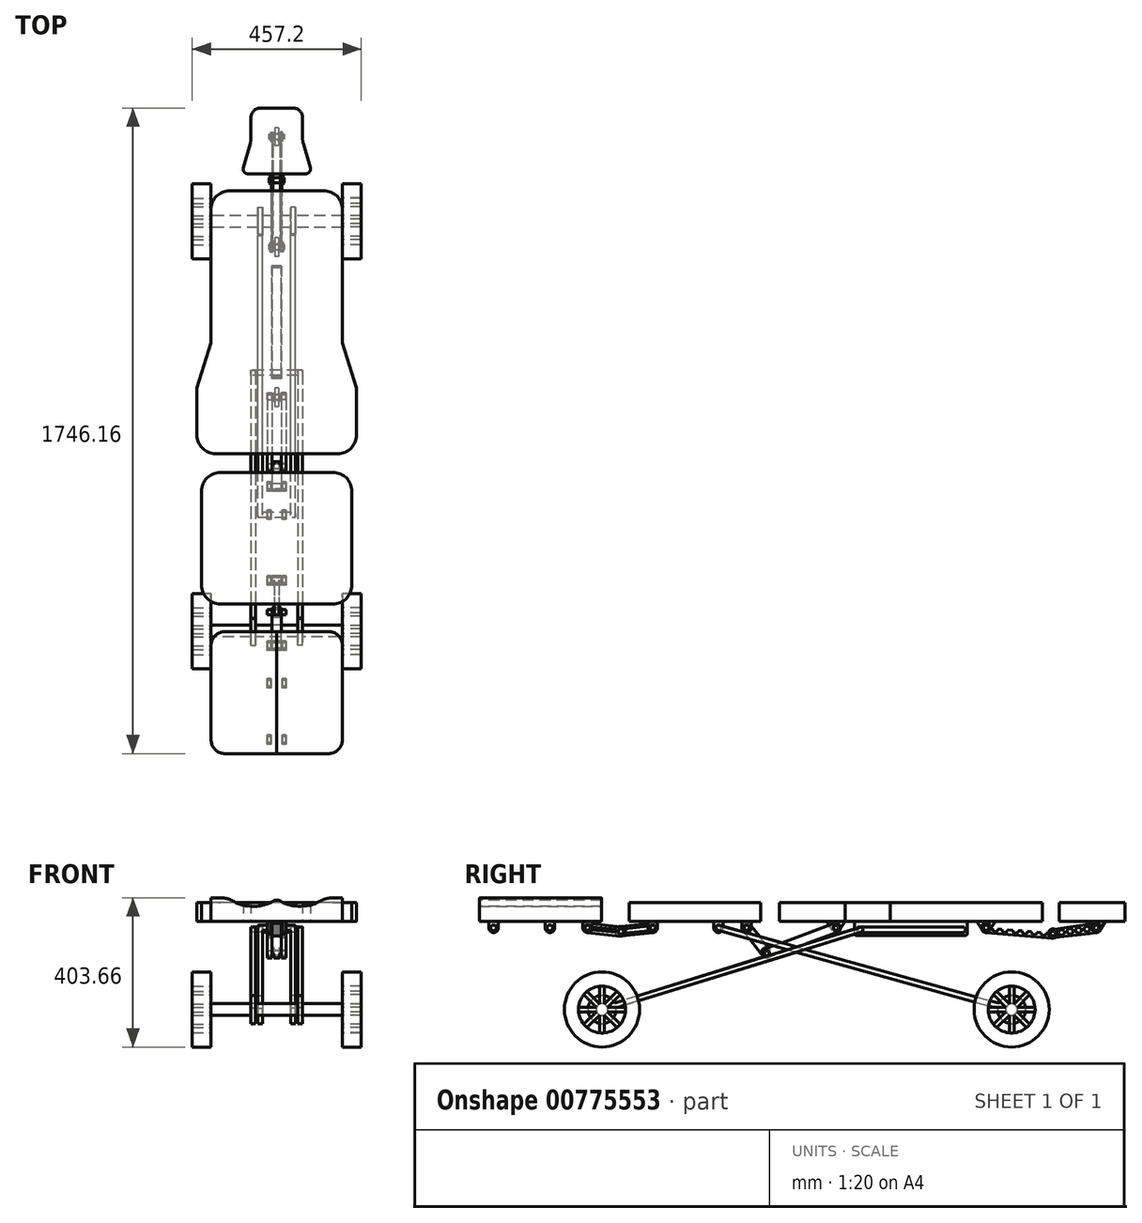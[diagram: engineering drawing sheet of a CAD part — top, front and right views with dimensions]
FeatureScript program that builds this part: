
annotation { "Feature Type Name" : "Feature", "Feature Type Description" : "" }
export const myFeature = defineFeature(function(context is Context, id is Id, definition is map)
    precondition{}
    {
        {
            var Q0;
            Q0=qCreatedBy(makeId("Top.planeOp"),FACE);
            var sketch = newSketch(context, id + "F0", { "sketchPlane" : qUnion([Q0])});
            skLineSegment(sketch, "E0.top", {"start": v(165.1, -355.6) * mm, "end": v(-165.1, -355.6) * mm});
            skLineSegment(sketch, "E0.left", {"start": v(215.9, -177.8) * mm, "end": v(215.9, -304.8) * mm});
            skLineSegment(sketch, "E0.right", {"start": v(-215.9, -177.8) * mm, "end": v(-215.9, -304.8) * mm});
            skPoint(sketch, "E0.middle", {"position": v(0, 0) * mm});
            skLineSegment(sketch, "E1.bottom", {"start": v(127, 355.6) * mm, "end": v(-127, 355.6) * mm});
            skLineSegment(sketch, "E1.left", {"start": v(177.8, 304.8) * mm, "end": v(177.8, -56.4) * mm});
            skLineSegment(sketch, "E1.right", {"start": v(-177.8, 304.8) * mm, "end": v(-177.8, -56.4) * mm});
            skPoint(sketch, "E2.orphan", {"position": v(-177.8, -355.6) * mm});
            skPoint(sketch, "E3.orphan", {"position": v(177.8, -355.6) * mm});
            skPoint(sketch, "E4.orphan", {"position": v(-215.9, 355.6) * mm});
            skPoint(sketch, "E5.orphan", {"position": v(215.9, 355.6) * mm});
            skPoint(sketch, "E6.visualSharp", {"position": v(-215.9, -355.6) * mm});
            skArc(sketch, "E6.filletArc", {"start": v(-215.9, -304.8) * mm, "mid": v(-201.02, -340.72) * mm, "end": v(-165.1, -355.6) * mm});
            skPoint(sketch, "E7.visualSharp", {"position": v(215.9, -355.6) * mm});
            skArc(sketch, "E7.filletArc", {"start": v(165.1, -355.6) * mm, "mid": v(201.02, -340.72) * mm, "end": v(215.9, -304.8) * mm});
            skPoint(sketch, "E8.visualSharp", {"position": v(-177.8, 355.6) * mm});
            skArc(sketch, "E8.filletArc", {"start": v(-127, 355.6) * mm, "mid": v(-162.92, 340.72) * mm, "end": v(-177.8, 304.8) * mm});
            skPoint(sketch, "E9.visualSharp", {"position": v(177.8, 355.6) * mm});
            skArc(sketch, "E9.filletArc", {"start": v(177.8, 304.8) * mm, "mid": v(162.92, 340.72) * mm, "end": v(127, 355.6) * mm});
            skLineSegment(sketch, "E10", {"start": v(-215.9, -177.8) * mm, "end": v(-177.8, -56.4) * mm});
            skLineSegment(sketch, "E11", {"start": v(215.9, -177.8) * mm, "end": v(177.8, -56.4) * mm});
            skSolve(sketch);
        }
        {
            var Q0;
            Q0 = qSketchRegion(id + "F0", true);
            extrude(context, id + "F1", {"entities" : qUnion([Q0]), "depth" : 50.8 * mm, "offsetDistance" : 25.4 * mm});
        }
        {
            var Q0;
            Q0=makeQuery(id+"F1.opExtrude","CAP_FACE",FACE,{"disambiguationData":[OSD([sQuery(id+"F0.wireOp",EDGE,"E0.top"),sQuery(id+"F0.wireOp",EDGE,"E0.left"),sQuery(id+"F0.wireOp",EDGE,"E0.right"),sQuery(id+"F0.wireOp",EDGE,"E1.bottom"),sQuery(id+"F0.wireOp",EDGE,"E1.left"),sQuery(id+"F0.wireOp",EDGE,"E1.right"),sQuery(id+"F0.wireOp",EDGE,"E6.filletArc"),sQuery(id+"F0.wireOp",EDGE,"E7.filletArc"),sQuery(id+"F0.wireOp",EDGE,"E8.filletArc"),sQuery(id+"F0.wireOp",EDGE,"E9.filletArc"),sQuery(id+"F0.wireOp",EDGE,"E10"),sQuery(id+"F0.wireOp",EDGE,"E11")])],"isStart":true});
            var sketch = newSketch(context, id + "F2", { "sketchPlane" : qUnion([Q0])});
            skLineSegment(sketch, "E12.bottom", {"start": v(152.4, 762) * mm, "end": v(-152.4, 762) * mm});
            skLineSegment(sketch, "E12.top", {"start": v(152.4, 406.4) * mm, "end": v(-152.4, 406.4) * mm});
            skLineSegment(sketch, "E12.left", {"start": v(203.2, 711.2) * mm, "end": v(203.2, 457.2) * mm});
            skLineSegment(sketch, "E12.right", {"start": v(-203.2, 711.2) * mm, "end": v(-203.2, 457.2) * mm});
            skPoint(sketch, "E12.middle", {"position": v(0, 584.2) * mm});
            skPoint(sketch, "E13.visualSharp", {"position": v(-203.2, 406.4) * mm});
            skArc(sketch, "E13.filletArc", {"start": v(-203.2, 457.2) * mm, "mid": v(-188.32, 421.28) * mm, "end": v(-152.4, 406.4) * mm});
            skPoint(sketch, "E14.visualSharp", {"position": v(203.2, 406.4) * mm});
            skArc(sketch, "E14.filletArc", {"start": v(152.4, 406.4) * mm, "mid": v(188.32, 421.28) * mm, "end": v(203.2, 457.2) * mm});
            skPoint(sketch, "E15.visualSharp", {"position": v(203.2, 762) * mm});
            skPoint(sketch, "E16.visualSharp", {"position": v(-203.2, 762) * mm});
            skArc(sketch, "E17.filletArc", {"start": v(-152.4, 762) * mm, "mid": v(-188.32, 747.12) * mm, "end": v(-203.2, 711.2) * mm});
            skArc(sketch, "E18.filletArc", {"start": v(203.2, 711.2) * mm, "mid": v(188.32, 747.12) * mm, "end": v(152.4, 762) * mm});
            skSolve(sketch);
        }
        {
            var Q0;
            Q0 = qSketchRegion(id + "F2", true);
            extrude(context, id + "F3", {"entities" : qUnion([Q0]), "oppositeDirection" : true, "depth" : 50.8 * mm, "offsetDistance" : 25.4 * mm});
        }
        {
            var Q0;
            Q0=makeQuery(id+"F1.opExtrude","CAP_FACE",FACE,{"disambiguationData":[OSD([sQuery(id+"F0.wireOp",EDGE,"E0.top"),sQuery(id+"F0.wireOp",EDGE,"E0.left"),sQuery(id+"F0.wireOp",EDGE,"E0.right"),sQuery(id+"F0.wireOp",EDGE,"E1.bottom"),sQuery(id+"F0.wireOp",EDGE,"E1.left"),sQuery(id+"F0.wireOp",EDGE,"E1.right"),sQuery(id+"F0.wireOp",EDGE,"E6.filletArc"),sQuery(id+"F0.wireOp",EDGE,"E7.filletArc"),sQuery(id+"F0.wireOp",EDGE,"E8.filletArc"),sQuery(id+"F0.wireOp",EDGE,"E9.filletArc"),sQuery(id+"F0.wireOp",EDGE,"E10"),sQuery(id+"F0.wireOp",EDGE,"E11")])],"isStart":true});
            var sketch = newSketch(context, id + "F4", { "sketchPlane" : qUnion([Q0])});
            skLineSegment(sketch, "E19.bottom", {"start": v(69.85, -401.32) * mm, "end": v(-69.85, -401.32) * mm});
            skLineSegment(sketch, "E19.top", {"start": v(44.45, -579.12) * mm, "end": v(-44.45, -579.12) * mm});
            skLineSegment(sketch, "E19.left", {"start": v(69.85, -497.33) * mm, "end": v(69.85, -553.72) * mm});
            skLineSegment(sketch, "E19.right", {"start": v(-69.85, -497.33) * mm, "end": v(-69.85, -553.72) * mm});
            skPoint(sketch, "E19.middle", {"position": v(0, -490.22) * mm});
            skLineSegment(sketch, "E20", {"start": v(-69.85, -401.32) * mm, "end": v(-78.41, -401.32) * mm});
            skLineSegment(sketch, "E21", {"start": v(-90.62, -417.5) * mm, "end": v(-71.8, -483.38) * mm});
            skLineSegment(sketch, "E22", {"start": v(71.8, -483.38) * mm, "end": v(90.62, -417.5) * mm});
            skLineSegment(sketch, "E23", {"start": v(78.41, -401.32) * mm, "end": v(69.85, -401.32) * mm});
            skPoint(sketch, "E24.visualSharp", {"position": v(-69.85, -579.12) * mm});
            skArc(sketch, "E24.filletArc", {"start": v(-69.85, -553.72) * mm, "mid": v(-62.41, -571.68) * mm, "end": v(-44.45, -579.12) * mm});
            skPoint(sketch, "E25.visualSharp", {"position": v(69.85, -579.12) * mm});
            skArc(sketch, "E25.filletArc", {"start": v(44.45, -579.12) * mm, "mid": v(62.41, -571.68) * mm, "end": v(69.85, -553.72) * mm});
            skPoint(sketch, "E26.visualSharp", {"position": v(-95.25, -401.32) * mm});
            skArc(sketch, "E26.filletArc", {"start": v(-78.41, -401.32) * mm, "mid": v(-88.55, -406.37) * mm, "end": v(-90.62, -417.5) * mm});
            skPoint(sketch, "E27.visualSharp", {"position": v(95.25, -401.32) * mm});
            skArc(sketch, "E27.filletArc", {"start": v(90.62, -417.5) * mm, "mid": v(88.55, -406.37) * mm, "end": v(78.41, -401.32) * mm});
            skPoint(sketch, "E28.visualSharp", {"position": v(-69.85, -490.22) * mm});
            skArc(sketch, "E28.filletArc", {"start": v(-69.85, -497.33) * mm, "mid": v(-70.34, -490.29) * mm, "end": v(-71.8, -483.38) * mm});
            skPoint(sketch, "E29.visualSharp", {"position": v(69.85, -490.22) * mm});
            skArc(sketch, "E29.filletArc", {"start": v(71.8, -483.38) * mm, "mid": v(70.34, -490.29) * mm, "end": v(69.85, -497.33) * mm});
            skSolve(sketch);
        }
        {
            var Q0;
            Q0 = qSketchRegion(id + "F4", true);
            extrude(context, id + "F5", {"entities" : qUnion([Q0]), "oppositeDirection" : true, "depth" : 50.8 * mm, "offsetDistance" : 25.4 * mm});
        }
        {
            var Q0;
            Q0=makeQuery(id+"F3.opExtrude","CAP_FACE",FACE,{"disambiguationData":[OSD([sQuery(id+"F2.wireOp",EDGE,"E12.bottom"),sQuery(id+"F2.wireOp",EDGE,"E12.top"),sQuery(id+"F2.wireOp",EDGE,"E12.left"),sQuery(id+"F2.wireOp",EDGE,"E12.right"),sQuery(id+"F2.wireOp",EDGE,"E13.filletArc"),sQuery(id+"F2.wireOp",EDGE,"E14.filletArc"),sQuery(id+"F2.wireOp",EDGE,"E17.filletArc"),sQuery(id+"F2.wireOp",EDGE,"E18.filletArc")])],"isStart":true});
            var sketch = newSketch(context, id + "F6", { "sketchPlane" : qUnion([Q0])});
            skLineSegment(sketch, "E30.bottom", {"start": v(139.7, 836.84) * mm, "end": v(-139.7, 836.84) * mm});
            skLineSegment(sketch, "E30.top", {"start": v(139.7, 1167.04) * mm, "end": v(-139.7, 1167.04) * mm});
            skLineSegment(sketch, "E30.left", {"start": v(177.8, 874.94) * mm, "end": v(177.8, 1128.94) * mm});
            skLineSegment(sketch, "E30.right", {"start": v(-177.8, 874.94) * mm, "end": v(-177.8, 1128.94) * mm});
            skPoint(sketch, "E30.middle", {"position": v(0, 1001.94) * mm});
            skPoint(sketch, "E30.middle.positionSnap0", {"position": v(0, 762) * mm});
            skPoint(sketch, "E30.centerSnap0", {"position": v(0, 762) * mm});
            skPoint(sketch, "E31.visualSharp", {"position": v(-177.8, 836.84) * mm});
            skArc(sketch, "E31.filletArc", {"start": v(-177.8, 874.94) * mm, "mid": v(-166.64, 848) * mm, "end": v(-139.7, 836.84) * mm});
            skPoint(sketch, "E32.visualSharp", {"position": v(177.8, 836.84) * mm});
            skArc(sketch, "E32.filletArc", {"start": v(139.7, 836.84) * mm, "mid": v(166.64, 848) * mm, "end": v(177.8, 874.94) * mm});
            skPoint(sketch, "E33.visualSharp", {"position": v(-177.8, 1167.04) * mm});
            skArc(sketch, "E33.filletArc", {"start": v(-139.7, 1167.04) * mm, "mid": v(-166.64, 1155.88) * mm, "end": v(-177.8, 1128.94) * mm});
            skPoint(sketch, "E34.visualSharp", {"position": v(177.8, 1167.04) * mm});
            skArc(sketch, "E34.filletArc", {"start": v(177.8, 1128.94) * mm, "mid": v(166.64, 1155.88) * mm, "end": v(139.7, 1167.04) * mm});
            skSolve(sketch);
        }
        {
            var Q0;
            Q0 = qSketchRegion(id + "F6", true);
            extrude(context, id + "F7", {"entities" : qUnion([Q0]), "oppositeDirection" : true, "depth" : 63.5 * mm, "offsetDistance" : 25.4 * mm});
        }
        {
            var Q0;
            Q0=makeQuery(id+"F7.opExtrude","SWEPT_FACE",FACE,{"disambiguationData":[OSD([sQuery(id+"F6.wireOp",EDGE,"E30.top")])]});
            cPlane(context, id + "F8", {"entities" : qUnion([Q0]), "cplaneType" : CPlaneType.OFFSET, "offset" : 0 * mm, "width" : 152.4 * mm, "height" : 152.4 * mm});
        }
        {
            var Q0;
            Q0=qCreatedBy(id+"F8.planeOp",FACE);
            var sketch = newSketch(context, id + "F9", { "sketchPlane" : qUnion([Q0])});
            skEllipse(sketch, "E35", {"center": v(-63.5, 63.46) * mm, "majorRadius": 22.86 * mm, "minorRadius": 57.15 * mm, "majorAxis": v(0, -1)});
            skEllipse(sketch, "E36", {"center": v(63.5, 63.78) * mm, "majorRadius": 22.86 * mm, "minorRadius": 57.15 * mm, "majorAxis": v(0, -1)});
            skEllipse(sketch, "E37", {"center": v(0, 63.78) * mm, "majorRadius": 6.35 * mm, "minorRadius": 25.4 * mm, "majorAxis": v(0, -1)});
            skPoint(sketch, "E37.centerSnap0", {"position": v(6.35, 63.78) * mm});
            skSolve(sketch);
        }
        {
            var Q0;
            Q0 = qSketchRegion(id + "F9", true);
            extrude(context, id + "F10", {"entities" : qUnion([Q0]), "operationType" : NewBodyOperationType.REMOVE, "oppositeDirection" : true, "depth" : 330.2 * mm, "offsetDistance" : 25.4 * mm});
        }
        {
            var Q0;
            Q0=makeQuery(id+"F10.boolean.opBoolean","INTERSECT",EDGE,{"disambiguationData":[OD(0.0)],"derivedFrom":[makeQuery(id+"F7.opExtrude","CAP_FACE",FACE,{"disambiguationData":[OSD([sQuery(id+"F6.wireOp",EDGE,"E30.bottom"),sQuery(id+"F6.wireOp",EDGE,"E30.top"),sQuery(id+"F6.wireOp",EDGE,"E30.left"),sQuery(id+"F6.wireOp",EDGE,"E30.right"),sQuery(id+"F6.wireOp",EDGE,"E31.filletArc"),sQuery(id+"F6.wireOp",EDGE,"E32.filletArc"),sQuery(id+"F6.wireOp",EDGE,"E33.filletArc"),sQuery(id+"F6.wireOp",EDGE,"E34.filletArc")])],"isStart":false}),makeQuery(id+"F10.opExtrude","SWEPT_FACE",FACE,{"disambiguationData":[OSD([sQuery(id+"F9.wireOp",EDGE,"E35")])]})]});
            var Q1;
            Q1=makeQuery(id+"F10.boolean.opBoolean","INTERSECT",EDGE,{"disambiguationData":[OD(0.0)],"derivedFrom":[makeQuery(id+"F7.opExtrude","CAP_FACE",FACE,{"disambiguationData":[OSD([sQuery(id+"F6.wireOp",EDGE,"E30.bottom"),sQuery(id+"F6.wireOp",EDGE,"E30.top"),sQuery(id+"F6.wireOp",EDGE,"E30.left"),sQuery(id+"F6.wireOp",EDGE,"E30.right"),sQuery(id+"F6.wireOp",EDGE,"E31.filletArc"),sQuery(id+"F6.wireOp",EDGE,"E32.filletArc"),sQuery(id+"F6.wireOp",EDGE,"E33.filletArc"),sQuery(id+"F6.wireOp",EDGE,"E34.filletArc")])],"isStart":false}),makeQuery(id+"F10.opExtrude","SWEPT_FACE",FACE,{"disambiguationData":[OSD([sQuery(id+"F9.wireOp",EDGE,"E36")])]})]});
            fillet(context, id + "F11", {"entities" : qUnion([Q0, Q1]), "radius" : 76.2 * mm, "tangentPropagation" : true, "allowEdgeOverflow" : false});
        }
        {
            var Q0;
            {var subQ0=sQuery(id+"F9.wireOp",EDGE,"E37");var subQ1=sQuery(id+"F9.wireOp",EDGE,"E35");Q0=makeQuery(id+"F10.boolean.opBoolean","COPY",EDGE,{"derivedFrom":makeQuery(id+"F10.opExtrude","SWEPT_EDGE",EDGE,{"disambiguationData":[OSD([subQ1,subQ0]),TDD([makeQuery(id+"F9.imprint","INTERSECT",VERTEX,{"disambiguationData":[OD(1.0)],"derivedFrom":[subQ1,subQ0]})])]})});}
            var Q1;
            {var subQ0=sQuery(id+"F9.wireOp",EDGE,"E37");var subQ1=sQuery(id+"F9.wireOp",EDGE,"E36");Q1=makeQuery(id+"F10.boolean.opBoolean","COPY",EDGE,{"derivedFrom":makeQuery(id+"F10.opExtrude","SWEPT_EDGE",EDGE,{"disambiguationData":[OSD([subQ1,subQ0]),TDD([makeQuery(id+"F9.imprint","INTERSECT",VERTEX,{"disambiguationData":[OD(1.0)],"derivedFrom":[subQ1,subQ0]})])]})});}
            fillet(context, id + "F12", {"entities" : qUnion([Q0, Q1]), "radius" : 25.4 * mm, "tangentPropagation" : true, "allowEdgeOverflow" : false});
        }
        {
            var Q0;
            Q0=qCreatedBy(makeId("Right.planeOp"),FACE);
            var sketch = newSketch(context, id + "F13", { "sketchPlane" : qUnion([Q0])});
            skCircle(sketch, "E38", {"center": v(501.56, -17.78) * mm, "radius": 7.62 * mm});
            skCircle(sketch, "E39", {"center": v(501.56, -17.78) * mm, "radius": 11.43 * mm});
            skLineSegment(sketch, "E40", {"start": v(525.6, 0) * mm, "end": v(511.36, -23.67) * mm});
            skLineSegment(sketch, "E41", {"start": v(491.77, -23.67) * mm, "end": v(477.52, 0) * mm});
            skLineSegment(sketch, "E42", {"start": v(501.56, -17.78) * mm, "end": v(501.56, 0) * mm, "construction": true});
            skLineSegment(sketch, "E43", {"start": v(525.6, 0) * mm, "end": v(477.52, 0) * mm});
            skSolve(sketch);
        }
        {
            var Q0;
            {var subQ0=sQuery(id+"F13.wireOp",EDGE,"E40");Q0=makeQuery(id+"F13.imprint","IMPRINT",FACE,{"disambiguationData":[TD([[makeQuery(id+"F13.imprint","IMPRINT",EDGE,{"derivedFrom":subQ0}),-1.0]])]});}
            extrude(context, id + "F14", {"entities" : qUnion([Q0]), "operationType" : NewBodyOperationType.ADD, "endBound" : BoundingType.SYMMETRIC, "depth" : 10.16 * mm, "offsetDistance" : 25.4 * mm});
        }
        {
            var Q0;
            Q0=makeQuery(id+"F13.imprint","IMPRINT",FACE,{"disambiguationData":[TD([[makeQuery(id+"F13.imprint","IMPRINT",EDGE,{"derivedFrom":sQuery(id+"F13.wireOp",EDGE,"E38")}),-1.0]])]});
            var Q1;
            Q1=sQuery(id+"F13.wireOp",EDGE,"E39");
            var Q2;
            Q2=sQuery(id+"F13.wireOp",EDGE,"E38");
            extrude(context, id + "F15", {"entities" : qUnion([Q0]), "operationType" : NewBodyOperationType.ADD, "surfaceOperationType" : NewSurfaceOperationType.ADD, "surfaceEntities" : qUnion([Q1, Q2]), "endBound" : BoundingType.SYMMETRIC, "depth" : 15.24 * mm, "offsetDistance" : 25.4 * mm});
        }
        {
            var Q0;
            Q0=qCreatedBy(makeId("Right.planeOp"),FACE);
            var sketch = newSketch(context, id + "F16", { "sketchPlane" : qUnion([Q0])});
            skCircle(sketch, "E44", {"center": v(203.2, -17.78) * mm, "radius": 7.62 * mm});
            skCircle(sketch, "E45", {"center": v(203.2, -17.78) * mm, "radius": 11.43 * mm});
            skCircle(sketch, "E46", {"center": v(-203.2, -17.78) * mm, "radius": 7.62 * mm});
            skCircle(sketch, "E47", {"center": v(-203.2, -17.78) * mm, "radius": 11.43 * mm});
            skLineSegment(sketch, "E48", {"start": v(203.2, -17.78) * mm, "end": v(203.2, 0) * mm, "construction": true});
            skLineSegment(sketch, "E49", {"start": v(228.6, 0) * mm, "end": v(212.75, -24.07) * mm});
            skLineSegment(sketch, "E50", {"start": v(193.65, -24.07) * mm, "end": v(177.8, 0) * mm});
            skLineSegment(sketch, "E51", {"start": v(-177.8, 0) * mm, "end": v(-193.65, -24.07) * mm});
            skLineSegment(sketch, "E52", {"start": v(-212.75, -24.07) * mm, "end": v(-228.6, 0) * mm});
            skLineSegment(sketch, "E53", {"start": v(228.6, 0) * mm, "end": v(177.8, 0) * mm});
            skLineSegment(sketch, "E54", {"start": v(-177.8, 0) * mm, "end": v(-228.6, 0) * mm});
            skLineSegment(sketch, "E55", {"start": v(-203.2, -17.78) * mm, "end": v(-203.2, 0) * mm, "construction": true});
            skSolve(sketch);
        }
        {
            var Q0;
            {var subQ0=sQuery(id+"F16.wireOp",EDGE,"E49");Q0=makeQuery(id+"F16.imprint","IMPRINT",FACE,{"disambiguationData":[TD([[makeQuery(id+"F16.imprint","IMPRINT",EDGE,{"derivedFrom":subQ0}),-1.0]])]});}
            var Q1;
            {var subQ0=sQuery(id+"F16.wireOp",EDGE,"E51");Q1=makeQuery(id+"F16.imprint","IMPRINT",FACE,{"disambiguationData":[TD([[makeQuery(id+"F16.imprint","IMPRINT",EDGE,{"derivedFrom":subQ0}),-1.0]])]});}
            extrude(context, id + "F17", {"entities" : qUnion([Q0, Q1]), "operationType" : NewBodyOperationType.ADD, "endBound" : BoundingType.SYMMETRIC, "depth" : 10.16 * mm, "offsetDistance" : 25.4 * mm});
        }
        {
            var Q0;
            Q0=makeQuery(id+"F16.imprint","IMPRINT",FACE,{"disambiguationData":[TD([[makeQuery(id+"F16.imprint","IMPRINT",EDGE,{"derivedFrom":sQuery(id+"F16.wireOp",EDGE,"E44")}),-1.0]])]});
            var Q1;
            Q1=makeQuery(id+"F16.imprint","IMPRINT",FACE,{"disambiguationData":[TD([[makeQuery(id+"F16.imprint","IMPRINT",EDGE,{"derivedFrom":sQuery(id+"F16.wireOp",EDGE,"E46")}),-1.0]])]});
            extrude(context, id + "F18", {"entities" : qUnion([Q0, Q1]), "operationType" : NewBodyOperationType.ADD, "endBound" : BoundingType.SYMMETRIC, "depth" : 15.24 * mm, "offsetDistance" : 25.4 * mm});
        }
        {
            var Q0;
            Q0=qCreatedBy(makeId("Right.planeOp"),FACE);
            var sketch = newSketch(context, id + "F19", { "sketchPlane" : qUnion([Q0])});
            skLineSegment(sketch, "E56.bottom", {"start": v(-147.32, -38.1) * mm, "end": v(147.32, -38.1) * mm});
            skLineSegment(sketch, "E56.left", {"start": v(-152.4, -33.02) * mm, "end": v(-152.4, 0) * mm});
            skLineSegment(sketch, "E56.right", {"start": v(152.4, -33.02) * mm, "end": v(152.4, 0) * mm});
            skPoint(sketch, "E56.middle", {"position": v(0, -22.86) * mm});
            skLineSegment(sketch, "E57.bottom", {"start": v(-139.7, -30.48) * mm, "end": v(139.7, -30.48) * mm});
            skLineSegment(sketch, "E57.top", {"start": v(-139.7, -15.24) * mm, "end": v(139.7, -15.24) * mm});
            skLineSegment(sketch, "E58", {"start": v(152.4, 0) * mm, "end": v(-152.4, 0) * mm});
            skPoint(sketch, "E59.orphan", {"position": v(-152.4, -7.62) * mm});
            skPoint(sketch, "E60.orphan", {"position": v(152.4, -7.62) * mm});
            skLineSegment(sketch, "E61", {"start": v(0, 0) * mm, "end": v(0, -38.1) * mm, "construction": true});
            skPoint(sketch, "E62.visualSharp", {"position": v(144.78, -30.48) * mm});
            skPoint(sketch, "E63.visualSharp", {"position": v(144.78, -15.24) * mm});
            skPoint(sketch, "E64.visualSharp", {"position": v(-144.78, -30.48) * mm});
            skPoint(sketch, "E65.visualSharp", {"position": v(-144.78, -15.24) * mm});
            skPoint(sketch, "E66.visualSharp", {"position": v(152.4, -38.1) * mm});
            skArc(sketch, "E66.filletArc", {"start": v(147.32, -38.1) * mm, "mid": v(150.91, -36.61) * mm, "end": v(152.4, -33.02) * mm});
            skPoint(sketch, "E67.visualSharp", {"position": v(-152.4, -38.1) * mm});
            skArc(sketch, "E67.filletArc", {"start": v(-152.4, -33.02) * mm, "mid": v(-150.91, -36.61) * mm, "end": v(-147.32, -38.1) * mm});
            skArc(sketch, "E68", {"start": v(-139.7, -15.24) * mm, "mid": v(-147.32, -22.86) * mm, "end": v(-139.7, -30.48) * mm});
            skArc(sketch, "E69", {"start": v(139.7, -30.48) * mm, "mid": v(147.32, -22.86) * mm, "end": v(139.7, -15.24) * mm});
            skSolve(sketch);
        }
        {
            var Q0;
            Q0=makeQuery(id+"F19.imprint","IMPRINT",FACE,{"disambiguationData":[TD([[makeQuery(id+"F19.imprint","IMPRINT",EDGE,{"derivedFrom":sQuery(id+"F19.wireOp",EDGE,"E56.bottom")}),1.0]])]});
            extrude(context, id + "F20", {"entities" : qUnion([Q0]), "operationType" : NewBodyOperationType.ADD, "endBound" : BoundingType.SYMMETRIC, "depth" : 25.4 * mm, "offsetDistance" : 25.4 * mm});
        }
        {
            var Q0;
            Q0=makeQuery(id+"F18.opExtrude","CAP_FACE",FACE,{"disambiguationData":[OSD([sQuery(id+"F16.wireOp",EDGE,"E44"),sQuery(id+"F16.wireOp",EDGE,"E45")])],"isStart":false});
            cPlane(context, id + "F21", {"entities" : qUnion([Q0]), "cplaneType" : CPlaneType.OFFSET, "offset" : 2.54 * mm, "width" : 152.4 * mm, "height" : 152.4 * mm});
        }
        {
            var Q0;
            Q0=qCreatedBy(id+"F21.planeOp",FACE);
            var sketch = newSketch(context, id + "F22", { "sketchPlane" : qUnion([Q0])});
            skCircle(sketch, "E70", {"center": v(203.2, -17.78) * mm, "radius": 7.62 * mm});
            skCircle(sketch, "E71", {"center": v(203.2, -17.78) * mm, "radius": 12.7 * mm});
            skCircle(sketch, "E72", {"center": v(501.4, -17.78) * mm, "radius": 7.62 * mm});
            skCircle(sketch, "E73", {"center": v(501.4, -17.78) * mm, "radius": 12.7 * mm});
            skLineSegment(sketch, "E74", {"start": v(501.4, 0) * mm, "end": v(501.4, -17.78) * mm, "construction": true});
            skLineSegment(sketch, "E75", {"start": v(203.2, -17.78) * mm, "end": v(203.2, 0) * mm, "construction": true});
            skLineSegment(sketch, "E76", {"start": v(203.2, -5.08) * mm, "end": v(384.33, -20.64) * mm});
            skLineSegment(sketch, "E77", {"start": v(384.33, -20.64) * mm, "end": v(501.4, -5.08) * mm});
            skCircle(sketch, "E78", {"center": v(384.33, -33.34) * mm, "radius": 12.7 * mm});
            skLineSegment(sketch, "E79", {"start": v(203.2, -30.48) * mm, "end": v(383.24, -46) * mm});
            skLineSegment(sketch, "E80", {"start": v(383.24, -46) * mm, "end": v(501.4, -30.48) * mm});
            skCircle(sketch, "E81", {"center": v(384.33, -33.34) * mm, "radius": 7.62 * mm});
            skCircle(sketch, "E82", {"center": v(359.02, -31.21) * mm, "radius": 7.62 * mm});
            skCircle(sketch, "E83", {"center": v(333.71, -29.08) * mm, "radius": 7.62 * mm});
            skCircle(sketch, "E84", {"center": v(308.4, -26.95) * mm, "radius": 7.62 * mm});
            skCircle(sketch, "E85", {"center": v(283.41, -24.85) * mm, "radius": 7.62 * mm});
            skCircle(sketch, "E86", {"center": v(253.76, -22.63) * mm, "radius": 7.62 * mm});
            skCircle(sketch, "E87", {"center": v(228.44, -20.58) * mm, "radius": 7.62 * mm});
            skLineSegment(sketch, "E88", {"start": v(384.33, -33.34) * mm, "end": v(203.2, -17.78) * mm});
            skLineSegment(sketch, "E89", {"start": v(501.4, -17.78) * mm, "end": v(384.33, -33.34) * mm, "construction": true});
            skCircle(sketch, "E90", {"center": v(476, -21.16) * mm, "radius": 7.62 * mm});
            skCircle(sketch, "E91", {"center": v(453.14, -24.2) * mm, "radius": 7.62 * mm});
            skCircle(sketch, "E92", {"center": v(430.28, -27.23) * mm, "radius": 7.62 * mm});
            skCircle(sketch, "E93", {"center": v(407.42, -30.27) * mm, "radius": 7.62 * mm});
            skSolve(sketch);
        }
        {
            var Q0;
            {var subQ20=sQuery(id+"F22.wireOp",EDGE,"E79");Q0=makeQuery(id+"F22.imprint","IMPRINT",FACE,{"disambiguationData":[TD([[makeQuery(id+"F22.imprint","IMPRINT",EDGE,{"derivedFrom":subQ20}),1.0]])]});}
            var Q1;
            {var subQ10=sQuery(id+"F22.wireOp",EDGE,"E76");var subQ11=sQuery(id+"F22.wireOp",EDGE,"E71");var subQ12=makeQuery(id+"F22.imprint","INTERSECT",VERTEX,{"disambiguationData":[OD(1.0)],"derivedFrom":[subQ11,subQ10]});Q1=makeQuery(id+"F22.imprint","IMPRINT",FACE,{"disambiguationData":[TD([[makeQuery(id+"F22.imprint","IMPRINT",EDGE,{"disambiguationData":[TD([[subQ12,1.0]])],"derivedFrom":subQ11}),-1.0]])]});}
            extrude(context, id + "F23", {"entities" : qUnion([Q0, Q1]), "depth" : 3.8 * mm, "offsetDistance" : 25.4 * mm});
        }
        {
            var Q0;
            Q0=makeQuery(id+"F22.imprint","IMPRINT",FACE,{"disambiguationData":[TD([[makeQuery(id+"F22.imprint","IMPRINT",EDGE,{"derivedFrom":sQuery(id+"F22.wireOp",EDGE,"E81")}),-1.0]])]});
            var Q1;
            Q1=makeQuery(id+"F22.imprint","IMPRINT",FACE,{"disambiguationData":[TD([[makeQuery(id+"F22.imprint","IMPRINT",EDGE,{"derivedFrom":sQuery(id+"F22.wireOp",EDGE,"E70")}),-1.0]])]});
            extrude(context, id + "F24", {"entities" : qUnion([Q0, Q1]), "operationType" : NewBodyOperationType.ADD, "depth" : 7.62 * mm, "offsetDistance" : 25.4 * mm});
        }
        {
            var Q0;
            Q0=makeQuery(id+"F22.imprint","IMPRINT",FACE,{"disambiguationData":[TD([[makeQuery(id+"F22.imprint","IMPRINT",EDGE,{"derivedFrom":sQuery(id+"F22.wireOp",EDGE,"E81")}),-1.0]])]});
            extrude(context, id + "F25", {"entities" : qUnion([Q0]), "operationType" : NewBodyOperationType.REMOVE, "depth" : 2.54 * mm, "offsetDistance" : 25.4 * mm});
        }
        {
            var Q0;
            Q0=makeQuery(id+"F22.imprint","IMPRINT",FACE,{"disambiguationData":[TD([[makeQuery(id+"F22.imprint","IMPRINT",EDGE,{"derivedFrom":sQuery(id+"F22.wireOp",EDGE,"E90")}),-1.0]])]});
            var sketch = newSketch(context, id + "F26", { "sketchPlane" : qUnion([Q0])});
            skCircle(sketch, "E94", {"center": v(384.17, -33.42) * mm, "radius": 11.43 * mm});
            skCircle(sketch, "E95", {"center": v(501.36, -17.97) * mm, "radius": 12.7 * mm});
            skCircle(sketch, "E96", {"center": v(407.63, -30.12) * mm, "radius": 7.62 * mm});
            skCircle(sketch, "E97", {"center": v(430.45, -27.47) * mm, "radius": 7.62 * mm});
            skCircle(sketch, "E98", {"center": v(453.67, -24.41) * mm, "radius": 7.62 * mm});
            skCircle(sketch, "E99", {"center": v(475.88, -21.36) * mm, "radius": 7.62 * mm});
            skLineSegment(sketch, "E100", {"start": v(501.33, -30.67) * mm, "end": v(384.17, -44.85) * mm});
            skLineSegment(sketch, "E101", {"start": v(384.17, -22) * mm, "end": v(501.36, -5.14) * mm});
            skCircle(sketch, "E102", {"center": v(384.17, -33.42) * mm, "radius": 7.62 * mm});
            skCircle(sketch, "E103", {"center": v(501.36, -17.97) * mm, "radius": 7.62 * mm});
            skSolve(sketch);
        }
        {
            var Q0;
            Q0=makeQuery(id+"F26.imprint","IMPRINT",FACE,{"disambiguationData":[TD([[makeQuery(id+"F26.imprint","IMPRINT",EDGE,{"derivedFrom":sQuery(id+"F26.wireOp",EDGE,"E103")}),-1.0]])]});
            var Q1;
            Q1=makeQuery(id+"F26.imprint","IMPRINT",FACE,{"disambiguationData":[TD([[makeQuery(id+"F26.imprint","IMPRINT",EDGE,{"derivedFrom":sQuery(id+"F26.wireOp",EDGE,"E102")}),-1.0]])]});
            var Q2;
            {var subQ26=sQuery(id+"F26.wireOp",EDGE,"E96");var subQ27=makeQuery(id+"F22.imprint","IMPRINT",EDGE,{"derivedFrom":sQuery(id+"F22.wireOp",EDGE,"E93")});var subQ28=makeQuery(id+"F26.imprint","INTERSECT",VERTEX,{"disambiguationData":[OD(0.0)],"derivedFrom":[subQ27,subQ26]});Q2=makeQuery(id+"F26.imprint","IMPRINT",FACE,{"disambiguationData":[TD([[makeQuery(id+"F26.imprint","IMPRINT",EDGE,{"disambiguationData":[TD([[subQ28,1.0]])],"derivedFrom":subQ26}),-1.0]])]});}
            var Q3;
            {var subQ0=sQuery(id+"F26.wireOp",EDGE,"E101");var subQ1=sQuery(id+"F26.wireOp",EDGE,"E94");var subQ2=makeQuery(id+"F26.imprint","INTERSECT",VERTEX,{"derivedFrom":[subQ1,subQ0]});Q3=makeQuery(id+"F26.imprint","IMPRINT",FACE,{"disambiguationData":[TD([[makeQuery(id+"F26.imprint","IMPRINT",EDGE,{"disambiguationData":[TD([[subQ2,1.0]])],"derivedFrom":subQ1}),-1.0]])]});}
            var Q4;
            {var subQ0=sQuery(id+"F26.wireOp",EDGE,"E95");var subQ1=sQuery(id+"F22.wireOp",EDGE,"E80");var subQ2=sQuery(id+"F22.wireOp",EDGE,"E73");var subQ3=makeQuery(id+"F22.imprint","INTERSECT",VERTEX,{"derivedFrom":[subQ2,subQ1]});var subQ4=makeQuery(id+"F22.imprint","IMPRINT",EDGE,{"disambiguationData":[TD([[subQ3,1.0]])],"derivedFrom":subQ2});var subQ5=makeQuery(id+"F26.imprint","INTERSECT",VERTEX,{"derivedFrom":[subQ4,subQ0]});Q4=makeQuery(id+"F26.imprint","IMPRINT",FACE,{"disambiguationData":[TD([[makeQuery(id+"F26.imprint","IMPRINT",EDGE,{"disambiguationData":[TD([[subQ5,-1.0]])],"derivedFrom":subQ0}),1.0]])]});}
            extrude(context, id + "F27", {"entities" : qUnion([Q0, Q1, Q2, Q3, Q4]), "depth" : 2.03 * mm, "offsetDistance" : 25.4 * mm});
        }
        {
            var Q0;
            Q0=makeQuery(id+"F26.imprint","IMPRINT",FACE,{"disambiguationData":[TD([[makeQuery(id+"F26.imprint","IMPRINT",EDGE,{"derivedFrom":sQuery(id+"F26.wireOp",EDGE,"E103")}),-1.0]])]});
            extrude(context, id + "F28", {"entities" : qUnion([Q0]), "operationType" : NewBodyOperationType.ADD, "depth" : 5.08 * mm, "offsetDistance" : 25.4 * mm});
        }
        {
            var Q0;
            Q0=makeQuery(id+"F18.opExtrude","CAP_FACE",FACE,{"disambiguationData":[OSD([sQuery(id+"F16.wireOp",EDGE,"E44"),sQuery(id+"F16.wireOp",EDGE,"E45")])],"isStart":true});
            cPlane(context, id + "F29", {"entities" : qUnion([Q0]), "cplaneType" : CPlaneType.OFFSET, "offset" : 7.62 * mm, "oppositeDirection" : true, "width" : 152.4 * mm, "height" : 152.4 * mm});
        }
        {
            var Q0;
            Q0=makeQuery(id+"F23.opExtrude","SWEPT_BODY",BODY,{"disambiguationData":[OSD([sQuery(id+"F22.wireOp",EDGE,"E71"),sQuery(id+"F22.wireOp",EDGE,"E76"),sQuery(id+"F22.wireOp",EDGE,"E78"),sQuery(id+"F22.wireOp",EDGE,"E79"),sQuery(id+"F22.wireOp",EDGE,"E82"),sQuery(id+"F22.wireOp",EDGE,"E83"),sQuery(id+"F22.wireOp",EDGE,"E84"),sQuery(id+"F22.wireOp",EDGE,"E85"),sQuery(id+"F22.wireOp",EDGE,"E86"),sQuery(id+"F22.wireOp",EDGE,"E87")])]});
            var Q1;
            Q1=qCreatedBy(id+"F29.planeOp",FACE);
            mirror(context, id + "F30", {"operationType" : NewBodyOperationType.ADD, "entities" : qUnion([Q0]), "mirrorPlane" : qUnion([Q1])});
        }
        {
            var Q0;
            Q0=makeQuery(id+"F27.opExtrude","SWEPT_BODY",BODY,{"disambiguationData":[OSD([sQuery(id+"F22.wireOp",EDGE,"E73"),sQuery(id+"F22.wireOp",EDGE,"E80"),sQuery(id+"F22.wireOp",EDGE,"E90"),sQuery(id+"F22.wireOp",EDGE,"E91"),sQuery(id+"F22.wireOp",EDGE,"E92"),sQuery(id+"F22.wireOp",EDGE,"E93"),sQuery(id+"F26.wireOp",EDGE,"E94"),sQuery(id+"F26.wireOp",EDGE,"E95"),sQuery(id+"F26.wireOp",EDGE,"E96"),sQuery(id+"F26.wireOp",EDGE,"E97"),sQuery(id+"F26.wireOp",EDGE,"E98"),sQuery(id+"F26.wireOp",EDGE,"E99"),sQuery(id+"F26.wireOp",EDGE,"E100"),sQuery(id+"F26.wireOp",EDGE,"E101"),sQuery(id+"F26.wireOp",EDGE,"E102"),sQuery(id+"F26.wireOp",EDGE,"E103")])]});
            var Q1;
            Q1=qCreatedBy(id+"F29.planeOp",FACE);
            mirror(context, id + "F31", {"entities" : qUnion([Q0]), "mirrorPlane" : qUnion([Q1])});
        }
        {
            var Q0;
            Q0=makeQuery(id+"F24.opExtrude","CAP_FACE",FACE,{"disambiguationData":[OSD([sQuery(id+"F22.wireOp",EDGE,"E78"),sQuery(id+"F22.wireOp",EDGE,"E80"),sQuery(id+"F22.wireOp",EDGE,"E81")])],"isStart":false});
            var sketch = newSketch(context, id + "F32", { "sketchPlane" : qUnion([Q0])});
            skCircle(sketch, "E104", {"center": v(384.33, -33.34) * mm, "radius": 6.99 * mm});
            skCircle(sketch, "E105", {"center": v(203.2, -17.78) * mm, "radius": 6.99 * mm});
            skCircle(sketch, "E106", {"center": v(501.36, -17.97) * mm, "radius": 6.99 * mm});
            skSolve(sketch);
        }
        {
            var Q0;
            Q0 = qSketchRegion(id + "F32", true);
            extrude(context, id + "F33", {"entities" : qUnion([Q0]), "oppositeDirection" : true, "depth" : 38.1 * mm, "offsetDistance" : 25.4 * mm, "hasSecondDirection" : true, "secondDirectionOppositeDirection" : false, "secondDirectionDepth" : 2.54 * mm});
        }
        {
            var Q0;
            Q0=makeQuery(id+"F3.opExtrude","SWEPT_FACE",FACE,{"disambiguationData":[OSD([sQuery(id+"F2.wireOp",EDGE,"E12.right")])]});
            var sketch = newSketch(context, id + "F34", { "sketchPlane" : qUnion([Q0])});
            skCircle(sketch, "E107", {"center": v(-272.27, -238.56) * mm, "radius": 101.6 * mm});
            skCircle(sketch, "E108", {"center": v(835.77, -238.56) * mm, "radius": 101.6 * mm});
            skCircle(sketch, "E109", {"center": v(-272.27, -238.56) * mm, "radius": 63.5 * mm});
            skCircle(sketch, "E110", {"center": v(835.77, -238.56) * mm, "radius": 63.5 * mm});
            skSolve(sketch);
        }
        {
            var Q0;
            Q0=qCreatedBy(makeId("Right.planeOp"),FACE);
            var sketch = newSketch(context, id + "F35", { "sketchPlane" : qUnion([Q0])});
            skCircle(sketch, "E111", {"center": v(-444.5, -17.78) * mm, "radius": 7.62 * mm});
            skCircle(sketch, "E112", {"center": v(-444.5, -17.78) * mm, "radius": 12.7 * mm});
            skCircle(sketch, "E113", {"center": v(-520.7, -17.78) * mm, "radius": 7.62 * mm});
            skCircle(sketch, "E114", {"center": v(-520.7, -17.78) * mm, "radius": 12.7 * mm});
            skCircle(sketch, "E115", {"center": v(-698.5, -17.78) * mm, "radius": 12.7 * mm});
            skCircle(sketch, "E116", {"center": v(-874.94, -17.78) * mm, "radius": 7.62 * mm});
            skCircle(sketch, "E117", {"center": v(-874.94, -17.78) * mm, "radius": 12.7 * mm});
            skCircle(sketch, "E118", {"center": v(-976.54, -17.78) * mm, "radius": 7.62 * mm});
            skCircle(sketch, "E119", {"center": v(-976.54, -17.78) * mm, "radius": 12.7 * mm});
            skCircle(sketch, "E120", {"center": v(-1128.94, -17.78) * mm, "radius": 7.62 * mm});
            skCircle(sketch, "E121", {"center": v(-1128.94, -17.78) * mm, "radius": 12.7 * mm});
            skCircle(sketch, "E122", {"center": v(-698.5, -17.78) * mm, "radius": 7.62 * mm});
            skLineSegment(sketch, "E123", {"start": v(-444.5, -17.78) * mm, "end": v(-444.5, 0) * mm, "construction": true});
            skLineSegment(sketch, "E124", {"start": v(-444.5, -17.78) * mm, "end": v(-520.7, -17.78) * mm, "construction": true});
            skLineSegment(sketch, "E125", {"start": v(-698.5, -17.78) * mm, "end": v(-520.7, -17.78) * mm, "construction": true});
            skLineSegment(sketch, "E126", {"start": v(-698.5, -17.78) * mm, "end": v(-711.2, -17.78) * mm, "construction": true});
            skLineSegment(sketch, "E127", {"start": v(-874.94, -17.78) * mm, "end": v(-976.54, -17.78) * mm, "construction": true});
            skLineSegment(sketch, "E128", {"start": v(-976.54, -17.78) * mm, "end": v(-1128.94, -17.78) * mm, "construction": true});
            skLineSegment(sketch, "E129.trimOffspring", {"start": v(-862.24, -17.78) * mm, "end": v(-874.94, -17.78) * mm, "construction": true});
            skLineSegment(sketch, "E130", {"start": v(-457.2, -17.78) * mm, "end": v(-457.2, 0) * mm});
            skLineSegment(sketch, "E131", {"start": v(-508, -17.78) * mm, "end": v(-508, 0) * mm});
            skLineSegment(sketch, "E132", {"start": v(-431.87, 0) * mm, "end": v(-457.2, 0) * mm});
            skLineSegment(sketch, "E133", {"start": v(-1141.64, -17.78) * mm, "end": v(-1141.64, 0) * mm});
            skLineSegment(sketch, "E134", {"start": v(-1116.24, -17.78) * mm, "end": v(-1116.24, 0) * mm});
            skLineSegment(sketch, "E135", {"start": v(-989.24, -17.78) * mm, "end": v(-989.24, 0) * mm});
            skLineSegment(sketch, "E136", {"start": v(-963.84, -17.78) * mm, "end": v(-963.84, 0) * mm});
            skLineSegment(sketch, "E137", {"start": v(-887.64, -17.78) * mm, "end": v(-887.64, 0) * mm});
            skLineSegment(sketch, "E138", {"start": v(-862.24, -17.78) * mm, "end": v(-862.24, 0) * mm});
            skLineSegment(sketch, "E139", {"start": v(-711.2, -17.78) * mm, "end": v(-711.2, 0) * mm});
            skLineSegment(sketch, "E140", {"start": v(-685.8, -17.78) * mm, "end": v(-685.8, 0) * mm});
            skLineSegment(sketch, "E141", {"start": v(-533.4, -17.78) * mm, "end": v(-533.4, 0) * mm});
            skPoint(sketch, "E142.orphan", {"position": v(-405.86, 0) * mm});
            skLineSegment(sketch, "E143.trimOffspring", {"start": v(-508, 0) * mm, "end": v(-533.4, 0) * mm});
            skLineSegment(sketch, "E144.trimOffspring", {"start": v(-685.8, 0) * mm, "end": v(-711.2, 0) * mm});
            skLineSegment(sketch, "E145.trimOffspring", {"start": v(-862.24, 0) * mm, "end": v(-887.64, 0) * mm});
            skLineSegment(sketch, "E146.trimOffspring", {"start": v(-963.84, 0) * mm, "end": v(-989.24, 0) * mm});
            skLineSegment(sketch, "E147.trimOffspring", {"start": v(-1116.24, 0) * mm, "end": v(-1141.64, 0) * mm});
            skLineSegment(sketch, "E148", {"start": v(-431.87, 0) * mm, "end": v(-431.8, -17.73) * mm});
            skSolve(sketch);
        }
        {
            var Q0;
            Q0 = qSketchRegion(id + "F35", true);
            extrude(context, id + "F36", {"entities" : qUnion([Q0]), "operationType" : NewBodyOperationType.ADD, "endBound" : BoundingType.SYMMETRIC, "depth" : 50.8 * mm, "offsetDistance" : 25.4 * mm});
        }
        {
            var Q0;
            Q0 = qSketchRegion(id + "F35", true);
            var Q1;
            Q1=sQuery(id+"F35.wireOp",EDGE,"E111");
            var Q2;
            Q2=sQuery(id+"F35.wireOp",EDGE,"E112");
            var Q3;
            Q3=sQuery(id+"F35.wireOp",EDGE,"E113");
            var Q4;
            Q4=sQuery(id+"F35.wireOp",EDGE,"E114");
            var Q5;
            Q5=sQuery(id+"F35.wireOp",EDGE,"E122");
            var Q6;
            Q6=sQuery(id+"F35.wireOp",EDGE,"E115");
            var Q7;
            Q7=sQuery(id+"F35.wireOp",EDGE,"E116");
            var Q8;
            Q8=sQuery(id+"F35.wireOp",EDGE,"E117");
            var Q9;
            Q9=sQuery(id+"F35.wireOp",EDGE,"E118");
            var Q10;
            Q10=sQuery(id+"F35.wireOp",EDGE,"E119");
            var Q11;
            Q11=sQuery(id+"F35.wireOp",EDGE,"E120");
            var Q12;
            Q12=sQuery(id+"F35.wireOp",EDGE,"E121");
            extrude(context, id + "F37", {"entities" : qUnion([Q0]), "operationType" : NewBodyOperationType.REMOVE, "surfaceEntities" : qUnion([Q1, Q2, Q3, Q4, Q5, Q6, Q7, Q8, Q9, Q10, Q11, Q12]), "endBound" : BoundingType.SYMMETRIC, "oppositeDirection" : true, "depth" : 30.48 * mm, "offsetDistance" : 25.4 * mm});
        }
        {
            var Q0;
            Q0=qCreatedBy(makeId("Right.planeOp"),FACE);
            var sketch = newSketch(context, id + "F38", { "sketchPlane" : qUnion([Q0])});
            skCircle(sketch, "E149", {"center": v(-444.5, -17.78) * mm, "radius": 7.62 * mm});
            skCircle(sketch, "E150", {"center": v(-203.2, -17.78) * mm, "radius": 6.99 * mm});
            skCircle(sketch, "E151", {"center": v(-390.02, -86.46) * mm, "radius": 7.62 * mm});
            skCircle(sketch, "E152", {"center": v(-390.02, -86.46) * mm, "radius": 12.7 * mm});
            skLineSegment(sketch, "E153", {"start": v(-203.2, -17.78) * mm, "end": v(-390.02, -86.46) * mm, "construction": true});
            skLineSegment(sketch, "E154", {"start": v(-390.02, -86.46) * mm, "end": v(-444.5, -17.78) * mm, "construction": true});
            skLineSegment(sketch, "E155.0", {"start": v(-380.07, -78.57) * mm, "end": v(-434.55, -9.89) * mm});
            skLineSegment(sketch, "E156.0", {"start": v(-399.97, -94.35) * mm, "end": v(-454.45, -25.67) * mm});
            skLineSegment(sketch, "E157.0", {"start": v(-207.58, -5.86) * mm, "end": v(-394.4, -74.54) * mm});
            skLineSegment(sketch, "E158.0", {"start": v(-198.82, -29.7) * mm, "end": v(-385.64, -98.38) * mm});
            skCircle(sketch, "E159", {"center": v(-444.5, -17.78) * mm, "radius": 12.7 * mm});
            skCircle(sketch, "E160", {"center": v(-203.2, -17.78) * mm, "radius": 12.7 * mm});
            skSolve(sketch);
        }
        {
            var Q0;
            {var subQ7=sQuery(id+"F38.wireOp",EDGE,"E156.0");Q0=makeQuery(id+"F38.imprint","IMPRINT",FACE,{"disambiguationData":[TD([[makeQuery(id+"F38.imprint","IMPRINT",EDGE,{"derivedFrom":subQ7}),-1.0]])]});}
            var Q1;
            {var subQ0=sQuery(id+"F38.wireOp",EDGE,"E155.0");var subQ1=sQuery(id+"F38.wireOp",EDGE,"E152");var subQ2=makeQuery(id+"F38.imprint","INTERSECT",VERTEX,{"derivedFrom":[subQ1,subQ0]});Q1=makeQuery(id+"F38.imprint","IMPRINT",FACE,{"disambiguationData":[TD([[makeQuery(id+"F38.imprint","IMPRINT",EDGE,{"disambiguationData":[TD([[subQ2,-1.0]])],"derivedFrom":subQ1}),-1.0]])]});}
            var Q2;
            Q2=makeQuery(id+"F38.imprint","IMPRINT",FACE,{"disambiguationData":[TD([[makeQuery(id+"F38.imprint","IMPRINT",EDGE,{"derivedFrom":sQuery(id+"F38.wireOp",EDGE,"E151")}),-1.0]])]});
            var Q3;
            Q3=makeQuery(id+"F38.imprint","IMPRINT",FACE,{"disambiguationData":[TD([[makeQuery(id+"F38.imprint","IMPRINT",EDGE,{"derivedFrom":sQuery(id+"F38.wireOp",EDGE,"E149")}),-1.0]])]});
            extrude(context, id + "F39", {"entities" : qUnion([Q0, Q1, Q2, Q3]), "endBound" : BoundingType.SYMMETRIC, "depth" : 25.4 * mm, "offsetDistance" : 25.4 * mm});
        }
        {
            var Q0;
            Q0=makeQuery(id+"F39.opExtrude","CAP_FACE",FACE,{"disambiguationData":[OSD([sQuery(id+"F38.wireOp",EDGE,"E149"),sQuery(id+"F38.wireOp",EDGE,"E151"),sQuery(id+"F38.wireOp",EDGE,"E152"),sQuery(id+"F38.wireOp",EDGE,"E155.0"),sQuery(id+"F38.wireOp",EDGE,"E156.0"),sQuery(id+"F38.wireOp",EDGE,"E159")])],"isStart":true});
            var sketch = newSketch(context, id + "F40", { "sketchPlane" : qUnion([Q0])});
            skCircle(sketch, "E161.0", {"center": v(390.02, -86.46) * mm, "radius": 7.62 * mm});
            skCircle(sketch, "E162", {"center": v(390.02, -86.46) * mm, "radius": 15.24 * mm});
            skSolve(sketch);
        }
        {
            var Q0;
            Q0 = qSketchRegion(id + "F40", true);
            extrude(context, id + "F41", {"entities" : qUnion([Q0]), "operationType" : NewBodyOperationType.REMOVE, "oppositeDirection" : true, "depth" : 5.08 * mm, "offsetDistance" : 25.4 * mm});
        }
        {
            var Q0;
            Q0=makeQuery(id+"F39.opExtrude","CAP_FACE",FACE,{"disambiguationData":[OSD([sQuery(id+"F38.wireOp",EDGE,"E149"),sQuery(id+"F38.wireOp",EDGE,"E151"),sQuery(id+"F38.wireOp",EDGE,"E152"),sQuery(id+"F38.wireOp",EDGE,"E155.0"),sQuery(id+"F38.wireOp",EDGE,"E156.0"),sQuery(id+"F38.wireOp",EDGE,"E159")])],"isStart":false});
            var sketch = newSketch(context, id + "F42", { "sketchPlane" : qUnion([Q0])});
            skCircle(sketch, "E163.0", {"center": v(-390.02, -86.46) * mm, "radius": 15.24 * mm});
            skCircle(sketch, "E164.0", {"center": v(-390.02, -86.46) * mm, "radius": 7.62 * mm});
            skSolve(sketch);
        }
        {
            var Q0;
            Q0 = qSketchRegion(id + "F42", true);
            extrude(context, id + "F43", {"entities" : qUnion([Q0]), "operationType" : NewBodyOperationType.REMOVE, "oppositeDirection" : true, "depth" : 5.08 * mm, "offsetDistance" : 25.4 * mm});
        }
        {
            var Q0;
            Q0=makeQuery(id+"F39.opExtrude","CAP_FACE",FACE,{"disambiguationData":[OSD([sQuery(id+"F38.wireOp",EDGE,"E149"),sQuery(id+"F38.wireOp",EDGE,"E151"),sQuery(id+"F38.wireOp",EDGE,"E152"),sQuery(id+"F38.wireOp",EDGE,"E155.0"),sQuery(id+"F38.wireOp",EDGE,"E156.0"),sQuery(id+"F38.wireOp",EDGE,"E159")])],"isStart":true});
            var sketch = newSketch(context, id + "F44", { "sketchPlane" : qUnion([Q0])});
            skLineSegment(sketch, "E165.0", {"start": v(207.58, -5.86) * mm, "end": v(394.4, -74.54) * mm});
            skLineSegment(sketch, "E166.0", {"start": v(198.82, -29.7) * mm, "end": v(385.64, -98.38) * mm});
            skCircle(sketch, "E167.0", {"center": v(203.2, -17.78) * mm, "radius": 12.7 * mm});
            skCircle(sketch, "E168.0", {"center": v(203.2, -17.78) * mm, "radius": 6.99 * mm});
            skCircle(sketch, "E169.0", {"center": v(390.02, -86.46) * mm, "radius": 12.7 * mm});
            skCircle(sketch, "E170.0", {"center": v(390.02, -86.46) * mm, "radius": 7.62 * mm});
            skSolve(sketch);
        }
        {
            var Q0;
            Q0 = qSketchRegion(id + "F44", true);
            extrude(context, id + "F45", {"entities" : qUnion([Q0]), "operationType" : NewBodyOperationType.ADD, "depth" : 12.7 * mm, "offsetDistance" : 25.4 * mm});
        }
        {
            var Q0;
            Q0=makeQuery(id+"F39.opExtrude","CAP_FACE",FACE,{"disambiguationData":[OSD([sQuery(id+"F38.wireOp",EDGE,"E149"),sQuery(id+"F38.wireOp",EDGE,"E151"),sQuery(id+"F38.wireOp",EDGE,"E152"),sQuery(id+"F38.wireOp",EDGE,"E155.0"),sQuery(id+"F38.wireOp",EDGE,"E156.0"),sQuery(id+"F38.wireOp",EDGE,"E159")])],"isStart":false});
            var sketch = newSketch(context, id + "F46", { "sketchPlane" : qUnion([Q0])});
            skLineSegment(sketch, "E171.0", {"start": v(-198.82, -29.7) * mm, "end": v(-385.64, -98.38) * mm});
            skCircle(sketch, "E172.0", {"center": v(-203.2, -17.78) * mm, "radius": 12.7 * mm});
            skCircle(sketch, "E173.0", {"center": v(-203.2, -17.78) * mm, "radius": 6.99 * mm});
            skLineSegment(sketch, "E174.0", {"start": v(-207.58, -5.86) * mm, "end": v(-394.4, -74.54) * mm});
            skCircle(sketch, "E175.0", {"center": v(-390.02, -86.46) * mm, "radius": 12.7 * mm});
            skCircle(sketch, "E176.0", {"center": v(-390.02, -86.46) * mm, "radius": 7.62 * mm});
            skSolve(sketch);
        }
        {
            var Q0;
            Q0 = qSketchRegion(id + "F46", true);
            extrude(context, id + "F47", {"entities" : qUnion([Q0]), "operationType" : NewBodyOperationType.ADD, "depth" : 12.7 * mm, "offsetDistance" : 25.4 * mm});
        }
        {
            var Q0;
            Q0=qCreatedBy(makeId("Right.planeOp"),FACE);
            var sketch = newSketch(context, id + "F48", { "sketchPlane" : qUnion([Q0])});
            skCircle(sketch, "E177", {"center": v(-698.5, -17.78) * mm, "radius": 7.62 * mm});
            skCircle(sketch, "E178", {"center": v(-874.94, -17.78) * mm, "radius": 7.62 * mm});
            skCircle(sketch, "E179", {"center": v(-784.67, -27.53) * mm, "radius": 7.62 * mm});
            skCircle(sketch, "E180", {"center": v(-698.5, -17.78) * mm, "radius": 12.7 * mm});
            skCircle(sketch, "E181", {"center": v(-784.67, -27.53) * mm, "radius": 12.7 * mm});
            skCircle(sketch, "E182", {"center": v(-874.94, -17.78) * mm, "radius": 12.7 * mm});
            skLineSegment(sketch, "E183", {"start": v(-698.5, -17.78) * mm, "end": v(-784.67, -27.53) * mm, "construction": true});
            skLineSegment(sketch, "E184", {"start": v(-874.94, -17.78) * mm, "end": v(-784.67, -27.53) * mm, "construction": true});
            skLineSegment(sketch, "E185.0", {"start": v(-877.35, -30.3) * mm, "end": v(-784.63, -40.3) * mm});
            skLineSegment(sketch, "E186.0", {"start": v(-873.58, -5.15) * mm, "end": v(-783.3, -14.9) * mm});
            skLineSegment(sketch, "E187.0", {"start": v(-700.64, -5.24) * mm, "end": v(-786.1, -14.9) * mm});
            skLineSegment(sketch, "E188.0", {"start": v(-696.36, -30.32) * mm, "end": v(-784.63, -40.3) * mm});
            skArc(sketch, "E189.0.startCap", {"start": v(-875.35, -21.57) * mm, "mid": v(-878.73, -17.37) * mm, "end": v(-874.53, -14) * mm});
            skArc(sketch, "E189.0.endCap", {"start": v(-784.26, -23.74) * mm, "mid": v(-780.88, -27.93) * mm, "end": v(-785.07, -31.31) * mm});
            skLineSegment(sketch, "E189.0.left", {"start": v(-874.53, -14) * mm, "end": v(-784.26, -23.74) * mm});
            skLineSegment(sketch, "E189.0.right", {"start": v(-875.35, -21.57) * mm, "end": v(-785.07, -31.31) * mm});
            skSolve(sketch);
        }
        {
            var Q0;
            {var subQ0=sQuery(id+"F48.wireOp",EDGE,"E188.0");var subQ1=sQuery(id+"F48.wireOp",EDGE,"E181");var subQ2=makeQuery(id+"F48.imprint","INTERSECT",VERTEX,{"derivedFrom":[subQ1,subQ0]});Q0=makeQuery(id+"F48.imprint","IMPRINT",FACE,{"disambiguationData":[TD([[makeQuery(id+"F48.imprint","IMPRINT",EDGE,{"disambiguationData":[TD([[subQ2,1.0]])],"derivedFrom":subQ1}),-1.0]])]});}
            var Q1;
            {var subQ0=sQuery(id+"F48.wireOp",EDGE,"E186.0");var subQ1=sQuery(id+"F48.wireOp",EDGE,"E181");var subQ2=makeQuery(id+"F48.imprint","INTERSECT",VERTEX,{"derivedFrom":[subQ1,subQ0]});Q1=makeQuery(id+"F48.imprint","IMPRINT",FACE,{"disambiguationData":[TD([[makeQuery(id+"F48.imprint","IMPRINT",EDGE,{"disambiguationData":[TD([[subQ2,-1.0]])],"derivedFrom":subQ1}),-1.0]])]});}
            var Q2;
            {var subQ0=sQuery(id+"F48.wireOp",EDGE,"E185.0");var subQ1=sQuery(id+"F48.wireOp",EDGE,"E181");var subQ2=makeQuery(id+"F48.imprint","INTERSECT",VERTEX,{"derivedFrom":[subQ1,subQ0]});Q2=makeQuery(id+"F48.imprint","IMPRINT",FACE,{"disambiguationData":[TD([[makeQuery(id+"F48.imprint","IMPRINT",EDGE,{"disambiguationData":[TD([[subQ2,1.0]])],"derivedFrom":subQ1}),-1.0]])]});}
            var Q3;
            {var subQ4=sQuery(id+"F48.wireOp",EDGE,"E189.0.left");var subQ5=sQuery(id+"F48.wireOp",EDGE,"E178");var subQ6=makeQuery(id+"F48.imprint","INTERSECT",VERTEX,{"derivedFrom":[subQ5,subQ4]});Q3=makeQuery(id+"F48.imprint","IMPRINT",FACE,{"disambiguationData":[TD([[makeQuery(id+"F48.imprint","IMPRINT",EDGE,{"disambiguationData":[TD([[subQ6,-1.0]])],"derivedFrom":subQ5}),-1.0]])]});}
            var Q4;
            {var subQ0=sQuery(id+"F48.wireOp",EDGE,"E187.0");var subQ1=sQuery(id+"F48.wireOp",EDGE,"E181");var subQ2=makeQuery(id+"F48.imprint","INTERSECT",VERTEX,{"derivedFrom":[subQ1,subQ0]});Q4=makeQuery(id+"F48.imprint","IMPRINT",FACE,{"disambiguationData":[TD([[makeQuery(id+"F48.imprint","IMPRINT",EDGE,{"disambiguationData":[TD([[subQ2,-1.0]])],"derivedFrom":subQ1}),-1.0]])]});}
            var Q5;
            {var subQ2=sQuery(id+"F48.wireOp",EDGE,"E189.0.left");var subQ8=sQuery(id+"F48.wireOp",EDGE,"E179");var subQ9=makeQuery(id+"F48.imprint","INTERSECT",VERTEX,{"derivedFrom":[subQ8,subQ2]});Q5=makeQuery(id+"F48.imprint","IMPRINT",FACE,{"disambiguationData":[TD([[makeQuery(id+"F48.imprint","IMPRINT",EDGE,{"disambiguationData":[TD([[subQ9,1.0]])],"derivedFrom":subQ8}),-1.0]])]});}
            var Q6;
            {var subQ0=sQuery(id+"F48.wireOp",EDGE,"E189.0.left");var subQ1=sQuery(id+"F48.wireOp",EDGE,"E179");var subQ2=makeQuery(id+"F48.imprint","INTERSECT",VERTEX,{"derivedFrom":[subQ1,subQ0]});Q6=makeQuery(id+"F48.imprint","IMPRINT",FACE,{"disambiguationData":[TD([[makeQuery(id+"F48.imprint","IMPRINT",EDGE,{"disambiguationData":[TD([[subQ2,-1.0]])],"derivedFrom":subQ1}),-1.0]])]});}
            var Q7;
            {var subQ0=sQuery(id+"F48.wireOp",EDGE,"E189.0.left");var subQ1=sQuery(id+"F48.wireOp",EDGE,"E178");var subQ2=makeQuery(id+"F48.imprint","INTERSECT",VERTEX,{"derivedFrom":[subQ1,subQ0]});Q7=makeQuery(id+"F48.imprint","IMPRINT",FACE,{"disambiguationData":[TD([[makeQuery(id+"F48.imprint","IMPRINT",EDGE,{"disambiguationData":[TD([[subQ2,1.0]])],"derivedFrom":subQ1}),-1.0]])]});}
            extrude(context, id + "F49", {"entities" : qUnion([Q0, Q1, Q2, Q3, Q4, Q5, Q6, Q7]), "endBound" : BoundingType.SYMMETRIC, "depth" : 25.4 * mm, "offsetDistance" : 25.4 * mm});
        }
        {
            var Q0;
            Q0=qCreatedBy(makeId("Right.planeOp"),FACE);
            var sketch = newSketch(context, id + "F50", { "sketchPlane" : qUnion([Q0])});
            skCircle(sketch, "E190.0", {"center": v(-784.67, -27.53) * mm, "radius": 7.62 * mm});
            skCircle(sketch, "E191", {"center": v(-784.67, -27.53) * mm, "radius": 15.24 * mm});
            skSolve(sketch);
        }
        {
            var Q0;
            Q0 = qSketchRegion(id + "F50", true);
            extrude(context, id + "F51", {"entities" : qUnion([Q0]), "operationType" : NewBodyOperationType.REMOVE, "endBound" : BoundingType.SYMMETRIC, "depth" : 15.24 * mm, "offsetDistance" : 25.4 * mm});
        }
        {
            var Q0;
            Q0=qCreatedBy(makeId("Right.planeOp"),FACE);
            var sketch = newSketch(context, id + "F52", { "sketchPlane" : qUnion([Q0])});
            skLineSegment(sketch, "E192.0", {"start": v(-699.93, -5.16) * mm, "end": v(-786.1, -14.9) * mm});
            skLineSegment(sketch, "E193.0", {"start": v(-696.36, -30.32) * mm, "end": v(-784.63, -40.3) * mm});
            skCircle(sketch, "E194.0", {"center": v(-784.67, -27.53) * mm, "radius": 12.7 * mm});
            skCircle(sketch, "E195.0", {"center": v(-784.67, -27.53) * mm, "radius": 7.62 * mm});
            skCircle(sketch, "E196.0", {"center": v(-698.5, -17.78) * mm, "radius": 12.7 * mm});
            skCircle(sketch, "E197.0", {"center": v(-698.5, -17.78) * mm, "radius": 7.62 * mm});
            skLineSegment(sketch, "E198.ReBZ.ReBZ", {"start": v(-698.5, -17.78) * mm, "end": v(-784.67, -27.53) * mm, "construction": true});
            skArc(sketch, "E198.0.startCap", {"start": v(-699.21, -11.47) * mm, "mid": v(-692.2, -17.07) * mm, "end": v(-697.79, -24.09) * mm});
            skArc(sketch, "E198.0.endCap", {"start": v(-783.95, -33.84) * mm, "mid": v(-790.98, -28.24) * mm, "end": v(-785.38, -21.22) * mm});
            skLineSegment(sketch, "E198.0.left", {"start": v(-697.79, -24.09) * mm, "end": v(-783.95, -33.84) * mm});
            skLineSegment(sketch, "E198.0.right", {"start": v(-699.21, -11.47) * mm, "end": v(-785.38, -21.22) * mm});
            skPoint(sketch, "E199.orphan", {"position": v(-700.64, -5.24) * mm});
            skLineSegment(sketch, "E200", {"start": v(-699.93, -5.16) * mm, "end": v(-699.89, -5.21) * mm});
            skSolve(sketch);
        }
        {
            var Q0;
            Q0 = qSketchRegion(id + "F52", true);
            var Q1;
            Q1=makeQuery(id+"F48.imprint","IMPRINT",FACE,{"disambiguationData":[TD([[makeQuery(id+"F48.imprint","IMPRINT",EDGE,{"derivedFrom":sQuery(id+"F48.wireOp",EDGE,"E177")}),-1.0]])]});
            var Q2;
            {var subQ0=sQuery(id+"F52.wireOp",EDGE,"E198.0.right");var subQ1=sQuery(id+"F52.wireOp",EDGE,"E194.0");var subQ2=makeQuery(id+"F52.imprint","INTERSECT",VERTEX,{"derivedFrom":[subQ1,subQ0]});Q2=makeQuery(id+"F52.imprint","IMPRINT",FACE,{"disambiguationData":[TD([[makeQuery(id+"F52.imprint","IMPRINT",EDGE,{"disambiguationData":[TD([[subQ2,1.0]])],"derivedFrom":subQ1}),1.0]])]});}
            extrude(context, id + "F53", {"entities" : qUnion([Q0, Q1, Q2]), "endBound" : BoundingType.SYMMETRIC, "depth" : 12.7 * mm, "offsetDistance" : 25.4 * mm});
        }
        {
            var Q0;
            Q0=qCreatedBy(makeId("Right.planeOp"),FACE);
            var sketch = newSketch(context, id + "F54", { "sketchPlane" : qUnion([Q0])});
            skCircle(sketch, "E201.0", {"center": v(-698.5, -17.78) * mm, "radius": 7.62 * mm});
            skArc(sketch, "E202.0", {"start": v(-697.07, -30.4) * mm, "mid": v(-685.88, -16.35) * mm, "end": v(-699.93, -5.16) * mm});
            skCircle(sketch, "E203.0", {"center": v(-698.5, -17.78) * mm, "radius": 12.7 * mm});
            skSolve(sketch);
        }
        {
            var Q0;
            Q0 = qSketchRegion(id + "F54", true);
            extrude(context, id + "F55", {"entities" : qUnion([Q0]), "operationType" : NewBodyOperationType.ADD, "endBound" : BoundingType.SYMMETRIC, "depth" : 25.4 * mm, "offsetDistance" : 25.4 * mm});
        }
        {
            var Q0;
            Q0 = qSketchRegion(id + "F34", true);
            extrude(context, id + "F56", {"entities" : qUnion([Q0]), "endBound" : BoundingType.SYMMETRIC, "oppositeDirection" : true, "depth" : 50.8 * mm, "offsetDistance" : 25.4 * mm});
        }
        {
            var Q0;
            Q0=qCreatedBy(makeId("Right.planeOp"),FACE);
            var sketch = newSketch(context, id + "F57", { "sketchPlane" : qUnion([Q0])});
            skCircle(sketch, "E204", {"center": v(272.27, -238.56) * mm, "radius": 38.1 * mm});
            skCircle(sketch, "E205", {"center": v(-835.77, -238.56) * mm, "radius": 38.1 * mm});
            skCircle(sketch, "E206", {"center": v(-137.16, -22.86) * mm, "radius": 6.99 * mm});
            skCircle(sketch, "E207", {"center": v(-520.7, -17.78) * mm, "radius": 6.99 * mm});
            skLineSegment(sketch, "E208", {"start": v(-137.16, -22.86) * mm, "end": v(-835.77, -238.56) * mm, "construction": true});
            skLineSegment(sketch, "E209", {"start": v(-520.7, -17.78) * mm, "end": v(272.27, -238.56) * mm, "construction": true});
            skLineSegment(sketch, "E210.0", {"start": v(-522.57, -24.5) * mm, "end": v(270.4, -245.29) * mm});
            skLineSegment(sketch, "E211.0", {"start": v(-518.83, -11.05) * mm, "end": v(274.14, -231.83) * mm});
            skLineSegment(sketch, "E212.0", {"start": v(-139.22, -16.19) * mm, "end": v(-837.83, -231.89) * mm});
            skLineSegment(sketch, "E213.0", {"start": v(-135.1, -29.53) * mm, "end": v(-833.7, -245.23) * mm});
            skSolve(sketch);
        }
        {
            var Q0;
            Q0=makeQuery(id+"F3.opExtrude","SWEPT_FACE",FACE,{"disambiguationData":[OSD([sQuery(id+"F2.wireOp",EDGE,"E12.left")])]});
            var sketch = newSketch(context, id + "F58", { "sketchPlane" : qUnion([Q0])});
            skCircle(sketch, "E214.0", {"center": v(-835.77, -238.56) * mm, "radius": 63.5 * mm});
            skCircle(sketch, "E215.0", {"center": v(-835.77, -238.56) * mm, "radius": 101.6 * mm});
            skCircle(sketch, "E216.0", {"center": v(272.27, -238.56) * mm, "radius": 63.5 * mm});
            skCircle(sketch, "E217.0", {"center": v(272.27, -238.56) * mm, "radius": 101.6 * mm});
            skSolve(sketch);
        }
        {
            var Q0;
            Q0 = qSketchRegion(id + "F58", true);
            extrude(context, id + "F59", {"entities" : qUnion([Q0]), "operationType" : NewBodyOperationType.ADD, "endBound" : BoundingType.SYMMETRIC, "depth" : 50.8 * mm, "offsetDistance" : 25.4 * mm});
        }
        {
            var Q0;
            Q0=makeQuery(id+"F3.opExtrude","SWEPT_FACE",FACE,{"disambiguationData":[OSD([sQuery(id+"F2.wireOp",EDGE,"E12.left")])]});
            var sketch = newSketch(context, id + "F60", { "sketchPlane" : qUnion([Q0])});
            skCircle(sketch, "E218.0", {"center": v(272.27, -238.56) * mm, "radius": 63.5 * mm});
            skCircle(sketch, "E219.0", {"center": v(-835.77, -238.56) * mm, "radius": 63.5 * mm});
            skLineSegment(sketch, "E220.0", {"start": v(-885.16, -278.97) * mm, "end": v(-851.1, -244.91) * mm});
            skLineSegment(sketch, "E221.0", {"start": v(-876.18, -287.95) * mm, "end": v(-842.12, -253.9) * mm});
            skLineSegment(sketch, "E222.0", {"start": v(-829.42, -302.06) * mm, "end": v(-829.42, -253.9) * mm});
            skLineSegment(sketch, "E223.0", {"start": v(-842.12, -302.06) * mm, "end": v(-842.12, -253.9) * mm});
            skLineSegment(sketch, "E224.0", {"start": v(-885.16, -198.15) * mm, "end": v(-851.1, -232.21) * mm});
            skLineSegment(sketch, "E225.0", {"start": v(-876.18, -189.17) * mm, "end": v(-842.12, -223.23) * mm});
            skLineSegment(sketch, "E226.0", {"start": v(-899.27, -244.91) * mm, "end": v(-851.1, -244.91) * mm});
            skLineSegment(sketch, "E227.0", {"start": v(-899.27, -232.21) * mm, "end": v(-851.1, -232.21) * mm});
            skLineSegment(sketch, "E228.0", {"start": v(278.62, -302.06) * mm, "end": v(278.62, -253.9) * mm});
            skLineSegment(sketch, "E229.0", {"start": v(231.86, -287.95) * mm, "end": v(265.92, -253.9) * mm});
            skLineSegment(sketch, "E230.0", {"start": v(335.77, -244.91) * mm, "end": v(287.6, -244.91) * mm});
            skLineSegment(sketch, "E231.0", {"start": v(222.88, -198.15) * mm, "end": v(256.94, -232.21) * mm});
            skLineSegment(sketch, "E232.0", {"start": v(265.92, -302.06) * mm, "end": v(265.92, -253.9) * mm});
            skLineSegment(sketch, "E233.0", {"start": v(222.88, -278.97) * mm, "end": v(256.94, -244.91) * mm});
            skLineSegment(sketch, "E234.0", {"start": v(335.77, -232.21) * mm, "end": v(287.6, -232.21) * mm});
            skLineSegment(sketch, "E235.0", {"start": v(231.86, -189.17) * mm, "end": v(265.92, -223.23) * mm});
            skLineSegment(sketch, "E236.trimOffspring", {"start": v(-829.42, -223.23) * mm, "end": v(-829.42, -175.06) * mm});
            skLineSegment(sketch, "E237.trimOffspring", {"start": v(-829.42, -223.23) * mm, "end": v(-795.36, -189.17) * mm});
            skLineSegment(sketch, "E238.trimOffspring", {"start": v(-842.12, -223.23) * mm, "end": v(-842.12, -175.06) * mm});
            skLineSegment(sketch, "E239.trimOffspring", {"start": v(-829.42, -253.9) * mm, "end": v(-795.36, -287.95) * mm});
            skLineSegment(sketch, "E240.trimOffspring", {"start": v(-820.44, -232.21) * mm, "end": v(-772.27, -232.21) * mm});
            skLineSegment(sketch, "E241.trimOffspring", {"start": v(-820.44, -232.21) * mm, "end": v(-786.38, -198.15) * mm});
            skLineSegment(sketch, "E242.trimOffspring", {"start": v(-820.44, -244.91) * mm, "end": v(-786.38, -278.97) * mm});
            skLineSegment(sketch, "E243.trimOffspring", {"start": v(-820.44, -244.91) * mm, "end": v(-772.27, -244.91) * mm});
            skLineSegment(sketch, "E244.trimOffspring", {"start": v(265.92, -223.23) * mm, "end": v(265.92, -175.06) * mm});
            skLineSegment(sketch, "E245.trimOffspring", {"start": v(256.94, -232.21) * mm, "end": v(208.77, -232.21) * mm});
            skLineSegment(sketch, "E246.trimOffspring", {"start": v(256.94, -244.91) * mm, "end": v(208.77, -244.91) * mm});
            skLineSegment(sketch, "E247.trimOffspring", {"start": v(278.62, -253.9) * mm, "end": v(312.68, -287.95) * mm});
            skLineSegment(sketch, "E248.trimOffspring", {"start": v(287.6, -244.91) * mm, "end": v(321.66, -278.97) * mm});
            skLineSegment(sketch, "E249.trimOffspring", {"start": v(287.6, -232.21) * mm, "end": v(321.66, -198.15) * mm});
            skLineSegment(sketch, "E250.trimOffspring", {"start": v(278.62, -223.23) * mm, "end": v(278.62, -175.06) * mm});
            skLineSegment(sketch, "E251.trimOffspring", {"start": v(278.62, -223.23) * mm, "end": v(312.68, -189.17) * mm});
            skSolve(sketch);
        }
        {
            var Q0;
            {var subQ3=sQuery(id+"F60.wireOp",EDGE,"E218.0");var subQ22=sQuery(id+"F60.wireOp",EDGE,"E249.trimOffspring");var subQ37=makeQuery(id+"F60.imprint","INTERSECT",VERTEX,{"derivedFrom":[subQ3,subQ22]});Q0=makeQuery(id+"F60.imprint","IMPRINT",FACE,{"disambiguationData":[TD([[makeQuery(id+"F60.imprint","IMPRINT",EDGE,{"disambiguationData":[TD([[subQ37,-1.0]])],"derivedFrom":subQ3}),1.0]])]});}
            var Q1;
            {var subQ0=sQuery(id+"F60.wireOp",EDGE,"E241.trimOffspring");var subQ3=sQuery(id+"F60.wireOp",EDGE,"E219.0");var subQ4=makeQuery(id+"F60.imprint","INTERSECT",VERTEX,{"derivedFrom":[subQ3,subQ0]});Q1=makeQuery(id+"F60.imprint","IMPRINT",FACE,{"disambiguationData":[TD([[makeQuery(id+"F60.imprint","IMPRINT",EDGE,{"disambiguationData":[TD([[subQ4,-1.0]])],"derivedFrom":subQ3}),1.0]])]});}
            extrude(context, id + "F61", {"entities" : qUnion([Q0, Q1]), "endBound" : BoundingType.SYMMETRIC, "depth" : 50.8 * mm, "offsetDistance" : 25.4 * mm});
        }
        {
            var Q0;
            Q0=makeQuery(id+"F3.opExtrude","SWEPT_FACE",FACE,{"disambiguationData":[OSD([sQuery(id+"F2.wireOp",EDGE,"E12.right")])]});
            var sketch = newSketch(context, id + "F62", { "sketchPlane" : qUnion([Q0])});
            skCircle(sketch, "E252.0", {"center": v(-272.27, -238.56) * mm, "radius": 63.5 * mm});
            skLineSegment(sketch, "E253.0.0", {"start": v(-278.62, -223.23) * mm, "end": v(-312.45, -189.4) * mm});
            skArc(sketch, "E253.0.1", {"start": v(-312.45, -189.4) * mm, "mid": v(-317.17, -193.66) * mm, "end": v(-321.43, -198.37) * mm});
            skLineSegment(sketch, "E253.0.2", {"start": v(-321.43, -198.37) * mm, "end": v(-287.6, -232.21) * mm});
            skLineSegment(sketch, "E253.0.3", {"start": v(-287.6, -232.21) * mm, "end": v(-335.45, -232.21) * mm});
            skArc(sketch, "E253.0.4", {"start": v(-335.45, -232.21) * mm, "mid": v(-335.77, -238.56) * mm, "end": v(-335.45, -244.91) * mm});
            skLineSegment(sketch, "E253.0.5", {"start": v(-335.45, -244.91) * mm, "end": v(-287.6, -244.91) * mm});
            skLineSegment(sketch, "E253.0.6", {"start": v(-287.6, -244.91) * mm, "end": v(-321.43, -278.75) * mm});
            skArc(sketch, "E253.0.7", {"start": v(-321.43, -278.75) * mm, "mid": v(-317.17, -283.46) * mm, "end": v(-312.45, -287.73) * mm});
            skLineSegment(sketch, "E253.0.8", {"start": v(-312.45, -287.73) * mm, "end": v(-278.62, -253.9) * mm});
            skLineSegment(sketch, "E253.0.9", {"start": v(-278.62, -253.9) * mm, "end": v(-278.62, -301.74) * mm});
            skArc(sketch, "E253.0.10", {"start": v(-278.62, -301.74) * mm, "mid": v(-272.27, -302.06) * mm, "end": v(-265.92, -301.74) * mm});
            skLineSegment(sketch, "E253.0.11", {"start": v(-265.92, -301.74) * mm, "end": v(-265.92, -253.9) * mm});
            skLineSegment(sketch, "E253.0.12", {"start": v(-265.92, -253.9) * mm, "end": v(-232.08, -287.73) * mm});
            skArc(sketch, "E253.0.13", {"start": v(-232.08, -287.73) * mm, "mid": v(-227.37, -283.46) * mm, "end": v(-223.1, -278.75) * mm});
            skLineSegment(sketch, "E253.0.14", {"start": v(-223.1, -278.75) * mm, "end": v(-256.94, -244.91) * mm});
            skLineSegment(sketch, "E253.0.15", {"start": v(-256.94, -244.91) * mm, "end": v(-209.09, -244.91) * mm});
            skArc(sketch, "E253.0.16", {"start": v(-209.09, -244.91) * mm, "mid": v(-208.77, -238.56) * mm, "end": v(-209.09, -232.21) * mm});
            skLineSegment(sketch, "E253.0.17", {"start": v(-209.09, -232.21) * mm, "end": v(-256.94, -232.21) * mm});
            skLineSegment(sketch, "E253.0.18", {"start": v(-256.94, -232.21) * mm, "end": v(-223.1, -198.37) * mm});
            skArc(sketch, "E253.0.19", {"start": v(-223.1, -198.37) * mm, "mid": v(-227.37, -193.66) * mm, "end": v(-232.08, -189.4) * mm});
            skLineSegment(sketch, "E253.0.20", {"start": v(-232.08, -189.4) * mm, "end": v(-265.92, -223.23) * mm});
            skLineSegment(sketch, "E253.0.21", {"start": v(-265.92, -223.23) * mm, "end": v(-265.92, -175.38) * mm});
            skArc(sketch, "E253.0.22", {"start": v(-265.92, -175.38) * mm, "mid": v(-272.27, -175.06) * mm, "end": v(-278.62, -175.38) * mm});
            skLineSegment(sketch, "E253.0.23", {"start": v(-278.62, -175.38) * mm, "end": v(-278.62, -223.23) * mm});
            skCircle(sketch, "E254.0", {"center": v(835.77, -238.56) * mm, "radius": 63.5 * mm});
            skLineSegment(sketch, "E255.0.0", {"start": v(820.44, -232.21) * mm, "end": v(772.59, -232.21) * mm});
            skArc(sketch, "E255.0.1", {"start": v(772.59, -232.21) * mm, "mid": v(772.27, -238.56) * mm, "end": v(772.59, -244.91) * mm});
            skLineSegment(sketch, "E255.0.2", {"start": v(772.59, -244.91) * mm, "end": v(820.44, -244.91) * mm});
            skLineSegment(sketch, "E255.0.3", {"start": v(820.44, -244.91) * mm, "end": v(786.6, -278.75) * mm});
            skArc(sketch, "E255.0.4", {"start": v(786.6, -278.75) * mm, "mid": v(790.87, -283.46) * mm, "end": v(795.58, -287.73) * mm});
            skLineSegment(sketch, "E255.0.5", {"start": v(795.58, -287.73) * mm, "end": v(829.42, -253.9) * mm});
            skLineSegment(sketch, "E255.0.6", {"start": v(829.42, -253.9) * mm, "end": v(829.42, -301.74) * mm});
            skArc(sketch, "E255.0.7", {"start": v(829.42, -301.74) * mm, "mid": v(835.77, -302.06) * mm, "end": v(842.12, -301.74) * mm});
            skLineSegment(sketch, "E255.0.8", {"start": v(842.12, -301.74) * mm, "end": v(842.12, -253.9) * mm});
            skLineSegment(sketch, "E255.0.9", {"start": v(842.12, -253.9) * mm, "end": v(875.95, -287.73) * mm});
            skArc(sketch, "E255.0.10", {"start": v(875.95, -287.73) * mm, "mid": v(880.67, -283.46) * mm, "end": v(884.93, -278.75) * mm});
            skLineSegment(sketch, "E255.0.11", {"start": v(884.93, -278.75) * mm, "end": v(851.1, -244.91) * mm});
            skLineSegment(sketch, "E255.0.12", {"start": v(851.1, -244.91) * mm, "end": v(898.95, -244.91) * mm});
            skArc(sketch, "E255.0.13", {"start": v(898.95, -244.91) * mm, "mid": v(899.27, -238.56) * mm, "end": v(898.95, -232.21) * mm});
            skLineSegment(sketch, "E255.0.14", {"start": v(898.95, -232.21) * mm, "end": v(851.1, -232.21) * mm});
            skLineSegment(sketch, "E255.0.15", {"start": v(851.1, -232.21) * mm, "end": v(884.93, -198.37) * mm});
            skArc(sketch, "E255.0.16", {"start": v(884.93, -198.37) * mm, "mid": v(880.67, -193.66) * mm, "end": v(875.95, -189.4) * mm});
            skLineSegment(sketch, "E255.0.17", {"start": v(875.95, -189.4) * mm, "end": v(842.12, -223.23) * mm});
            skLineSegment(sketch, "E255.0.18", {"start": v(842.12, -223.23) * mm, "end": v(842.12, -175.38) * mm});
            skArc(sketch, "E255.0.19", {"start": v(842.12, -175.38) * mm, "mid": v(835.77, -175.06) * mm, "end": v(829.42, -175.38) * mm});
            skLineSegment(sketch, "E255.0.20", {"start": v(829.42, -175.38) * mm, "end": v(829.42, -223.23) * mm});
            skLineSegment(sketch, "E255.0.21", {"start": v(829.42, -223.23) * mm, "end": v(795.58, -189.4) * mm});
            skArc(sketch, "E255.0.22", {"start": v(795.58, -189.4) * mm, "mid": v(790.87, -193.66) * mm, "end": v(786.6, -198.37) * mm});
            skLineSegment(sketch, "E255.0.23", {"start": v(786.6, -198.37) * mm, "end": v(820.44, -232.21) * mm});
            skSolve(sketch);
        }
        {
            var Q0;
            {var subQ11=sQuery(id+"F62.wireOp",EDGE,"E253.0.0");Q0=makeQuery(id+"F62.imprint","IMPRINT",FACE,{"disambiguationData":[TD([[makeQuery(id+"F62.imprint","IMPRINT",EDGE,{"derivedFrom":subQ11}),1.0]])]});}
            var Q1;
            {var subQ9=sQuery(id+"F62.wireOp",EDGE,"E255.0.0");Q1=makeQuery(id+"F62.imprint","IMPRINT",FACE,{"disambiguationData":[TD([[makeQuery(id+"F62.imprint","IMPRINT",EDGE,{"derivedFrom":subQ9}),1.0]])]});}
            extrude(context, id + "F63", {"entities" : qUnion([Q0, Q1]), "operationType" : NewBodyOperationType.ADD, "endBound" : BoundingType.SYMMETRIC, "depth" : 50.8 * mm, "offsetDistance" : 25.4 * mm});
        }
        {
            var Q0;
            Q0=makeQuery(id+"F45.opExtrude","CAP_FACE",FACE,{"disambiguationData":[OSD([sQuery(id+"F44.wireOp",EDGE,"E165.0"),sQuery(id+"F44.wireOp",EDGE,"E166.0"),sQuery(id+"F44.wireOp",EDGE,"E167.0"),sQuery(id+"F44.wireOp",EDGE,"E168.0"),sQuery(id+"F44.wireOp",EDGE,"E169.0"),sQuery(id+"F44.wireOp",EDGE,"E170.0")])],"isStart":false});
            cPlane(context, id + "F64", {"entities" : qUnion([Q0]), "cplaneType" : CPlaneType.OFFSET, "offset" : 12.7 * mm, "width" : 152.4 * mm, "height" : 152.4 * mm});
        }
        {
            var Q0;
            Q0=makeQuery(id+"F47.opExtrude","CAP_FACE",FACE,{"disambiguationData":[OSD([sQuery(id+"F46.wireOp",EDGE,"E171.0"),sQuery(id+"F46.wireOp",EDGE,"E172.0"),sQuery(id+"F46.wireOp",EDGE,"E173.0"),sQuery(id+"F46.wireOp",EDGE,"E174.0"),sQuery(id+"F46.wireOp",EDGE,"E175.0"),sQuery(id+"F46.wireOp",EDGE,"E176.0")])],"isStart":false});
            cPlane(context, id + "F65", {"entities" : qUnion([Q0]), "cplaneType" : CPlaneType.OFFSET, "offset" : 12.7 * mm, "width" : 152.4 * mm, "height" : 152.4 * mm});
        }
        {
            var Q0;
            Q0=qCreatedBy(id+"F64.planeOp",FACE);
            var sketch = newSketch(context, id + "F66", { "sketchPlane" : qUnion([Q0])});
            skCircle(sketch, "E256.0", {"center": v(520.7, -17.78) * mm, "radius": 6.99 * mm});
            skLineSegment(sketch, "E257.0", {"start": v(518.83, -11.05) * mm, "end": v(-274.14, -231.83) * mm});
            skLineSegment(sketch, "E258.0", {"start": v(522.57, -24.5) * mm, "end": v(-270.4, -245.29) * mm});
            skCircle(sketch, "E259.0", {"center": v(-272.27, -238.56) * mm, "radius": 38.1 * mm});
            skSolve(sketch);
        }
        {
            var Q0;
            Q0 = qSketchRegion(id + "F66", true);
            extrude(context, id + "F67", {"entities" : qUnion([Q0]), "depth" : 12.7 * mm, "offsetDistance" : 25.4 * mm});
        }
        {
            var Q0;
            Q0=qCreatedBy(id+"F65.planeOp",FACE);
            var sketch = newSketch(context, id + "F68", { "sketchPlane" : qUnion([Q0])});
            skCircle(sketch, "E260.0", {"center": v(-520.7, -17.78) * mm, "radius": 6.99 * mm});
            skLineSegment(sketch, "E261.0", {"start": v(-518.83, -11.05) * mm, "end": v(274.14, -231.83) * mm});
            skLineSegment(sketch, "E262.0", {"start": v(-522.57, -24.5) * mm, "end": v(270.4, -245.29) * mm});
            skCircle(sketch, "E263.0", {"center": v(272.27, -238.56) * mm, "radius": 38.1 * mm});
            skSolve(sketch);
        }
        {
            var Q0;
            Q0 = qSketchRegion(id + "F68", true);
            extrude(context, id + "F69", {"entities" : qUnion([Q0]), "operationType" : NewBodyOperationType.ADD, "depth" : 12.7 * mm, "offsetDistance" : 25.4 * mm});
        }
        {
            var Q0;
            Q0=makeQuery(id+"F67.opExtrude","CAP_FACE",FACE,{"disambiguationData":[OSD([sQuery(id+"F66.wireOp",EDGE,"E256.0"),sQuery(id+"F66.wireOp",EDGE,"E257.0"),sQuery(id+"F66.wireOp",EDGE,"E258.0"),sQuery(id+"F66.wireOp",EDGE,"E259.0")])],"isStart":false});
            cPlane(context, id + "F70", {"entities" : qUnion([Q0]), "cplaneType" : CPlaneType.OFFSET, "offset" : 6.35 * mm, "width" : 152.4 * mm, "height" : 152.4 * mm});
        }
        {
            var Q0;
            Q0=makeQuery(id+"F69.opExtrude","CAP_FACE",FACE,{"disambiguationData":[OSD([sQuery(id+"F68.wireOp",EDGE,"E260.0"),sQuery(id+"F68.wireOp",EDGE,"E261.0"),sQuery(id+"F68.wireOp",EDGE,"E262.0"),sQuery(id+"F68.wireOp",EDGE,"E263.0")])],"isStart":false});
            cPlane(context, id + "F71", {"entities" : qUnion([Q0]), "cplaneType" : CPlaneType.OFFSET, "offset" : 6.35 * mm, "width" : 152.4 * mm, "height" : 152.4 * mm});
        }
        {
            var Q0;
            Q0=qCreatedBy(id+"F71.planeOp",FACE);
            var sketch = newSketch(context, id + "F72", { "sketchPlane" : qUnion([Q0])});
            skCircle(sketch, "E264.0", {"center": v(-835.77, -238.56) * mm, "radius": 38.1 * mm});
            skLineSegment(sketch, "E265.0", {"start": v(-139.22, -16.19) * mm, "end": v(-837.83, -231.89) * mm});
            skLineSegment(sketch, "E266.0", {"start": v(-135.1, -29.53) * mm, "end": v(-833.7, -245.23) * mm});
            skCircle(sketch, "E267.0", {"center": v(-137.16, -22.86) * mm, "radius": 6.99 * mm});
            skSolve(sketch);
        }
        {
            var Q0;
            Q0 = qSketchRegion(id + "F72", true);
            extrude(context, id + "F73", {"entities" : qUnion([Q0]), "depth" : 12.7 * mm, "offsetDistance" : 25.4 * mm});
        }
        {
            var Q0;
            Q0=qCreatedBy(id+"F70.planeOp",FACE);
            var sketch = newSketch(context, id + "F74", { "sketchPlane" : qUnion([Q0])});
            skCircle(sketch, "E268.0", {"center": v(137.16, -22.86) * mm, "radius": 6.99 * mm});
            skLineSegment(sketch, "E269.0", {"start": v(139.22, -16.19) * mm, "end": v(837.83, -231.89) * mm});
            skLineSegment(sketch, "E270.0", {"start": v(135.1, -29.53) * mm, "end": v(833.7, -245.23) * mm});
            skCircle(sketch, "E271.0", {"center": v(835.77, -238.56) * mm, "radius": 38.1 * mm});
            skSolve(sketch);
        }
        {
            var Q0;
            Q0 = qSketchRegion(id + "F74", true);
            extrude(context, id + "F75", {"entities" : qUnion([Q0]), "operationType" : NewBodyOperationType.ADD, "depth" : 12.7 * mm, "offsetDistance" : 25.4 * mm});
        }
        {
            var Q0;
            Q0=makeQuery(id+"F75.opExtrude","CAP_FACE",FACE,{"disambiguationData":[OSD([sQuery(id+"F74.wireOp",EDGE,"E268.0"),sQuery(id+"F74.wireOp",EDGE,"E269.0"),sQuery(id+"F74.wireOp",EDGE,"E270.0"),sQuery(id+"F74.wireOp",EDGE,"E271.0")])],"isStart":false});
            var sketch = newSketch(context, id + "F76", { "sketchPlane" : qUnion([Q0])});
            skCircle(sketch, "E272.0", {"center": v(137.16, -22.86) * mm, "radius": 6.99 * mm});
            skSolve(sketch);
        }
        {
            var Q0;
            Q0 = qSketchRegion(id + "F76", true);
            var Q1;
            Q1=makeQuery(id+"F73.opExtrude","CAP_FACE",FACE,{"disambiguationData":[OSD([sQuery(id+"F72.wireOp",EDGE,"E264.0"),sQuery(id+"F72.wireOp",EDGE,"E265.0"),sQuery(id+"F72.wireOp",EDGE,"E266.0"),sQuery(id+"F72.wireOp",EDGE,"E267.0")])],"isStart":true});
            var Q2;
            Q2=makeQuery(id+"F73.opExtrude","SWEPT_BODY",BODY,{"disambiguationData":[OSD([sQuery(id+"F72.wireOp",EDGE,"E264.0"),sQuery(id+"F72.wireOp",EDGE,"E265.0"),sQuery(id+"F72.wireOp",EDGE,"E266.0"),sQuery(id+"F72.wireOp",EDGE,"E267.0")])]});
            extrude(context, id + "F77", {"entities" : qUnion([Q0, Q1]), "endBound" : BoundingType.UP_TO_BODY, "oppositeDirection" : true, "depth" : 25.4 * mm, "endBoundEntityBody" : qUnion([Q2]), "offsetDistance" : 25.4 * mm});
        }
        {
            var Q0;
            Q0=qCreatedBy(makeId("Right.planeOp"),FACE);
            var sketch = newSketch(context, id + "F78", { "sketchPlane" : qUnion([Q0])});
            skCircle(sketch, "E273.0", {"center": v(-520.7, -17.78) * mm, "radius": 6.99 * mm});
            skSolve(sketch);
        }
        {
            var Q0;
            Q0 = qSketchRegion(id + "F78", true);
            extrude(context, id + "F79", {"entities" : qUnion([Q0]), "operationType" : NewBodyOperationType.ADD, "endBound" : BoundingType.SYMMETRIC, "depth" : 76.2 * mm, "offsetDistance" : 25.4 * mm});
        }
        {
            var Q0;
            Q0=makeQuery(id+"F36.opExtrude","CAP_FACE",FACE,{"disambiguationData":[OSD([sQuery(id+"F35.wireOp",EDGE,"E111"),sQuery(id+"F35.wireOp",EDGE,"E112"),sQuery(id+"F35.wireOp",EDGE,"E130"),sQuery(id+"F35.wireOp",EDGE,"E132"),sQuery(id+"F35.wireOp",EDGE,"E148")])],"isStart":true});
            var sketch = newSketch(context, id + "F80", { "sketchPlane" : qUnion([Q0])});
            skCircle(sketch, "E274", {"center": v(444.5, -17.78) * mm, "radius": 6.99 * mm});
            skCircle(sketch, "E275", {"center": v(698.5, -17.78) * mm, "radius": 6.99 * mm});
            skCircle(sketch, "E276", {"center": v(784.67, -27.53) * mm, "radius": 6.99 * mm});
            skCircle(sketch, "E277", {"center": v(874.94, -17.78) * mm, "radius": 6.99 * mm});
            skSolve(sketch);
        }
        {
            var Q0;
            Q0 = qSketchRegion(id + "F80", true);
            extrude(context, id + "F81", {"entities" : qUnion([Q0]), "oppositeDirection" : true, "depth" : 50.8 * mm, "offsetDistance" : 25.4 * mm});
        }
        {
            var Q0;
            Q0=makeQuery(id+"F45.opExtrude","CAP_FACE",FACE,{"disambiguationData":[OSD([sQuery(id+"F44.wireOp",EDGE,"E165.0"),sQuery(id+"F44.wireOp",EDGE,"E166.0"),sQuery(id+"F44.wireOp",EDGE,"E167.0"),sQuery(id+"F44.wireOp",EDGE,"E168.0"),sQuery(id+"F44.wireOp",EDGE,"E169.0"),sQuery(id+"F44.wireOp",EDGE,"E170.0")])],"isStart":false});
            var sketch = newSketch(context, id + "F82", { "sketchPlane" : qUnion([Q0])});
            skCircle(sketch, "E278", {"center": v(203.2, -17.78) * mm, "radius": 6.35 * mm});
            skCircle(sketch, "E279", {"center": v(390.02, -86.46) * mm, "radius": 6.35 * mm});
            skSolve(sketch);
        }
        {
            var Q0;
            Q0 = qSketchRegion(id + "F82", true);
            extrude(context, id + "F83", {"entities" : qUnion([Q0]), "operationType" : NewBodyOperationType.ADD, "oppositeDirection" : true, "depth" : 50.8 * mm, "offsetDistance" : 25.4 * mm});
        }
        {
            var Q0;
            Q0=qCreatedBy(makeId("Right.planeOp"),FACE);
            var sketch = newSketch(context, id + "F84", { "sketchPlane" : qUnion([Q0])});
            skCircle(sketch, "E280", {"center": v(272.27, -238.56) * mm, "radius": 15.88 * mm});
            skCircle(sketch, "E281", {"center": v(-835.77, -238.56) * mm, "radius": 15.88 * mm});
            skSolve(sketch);
        }
        {
            var Q0;
            Q0 = qSketchRegion(id + "F84", true);
            extrude(context, id + "F85", {"entities" : qUnion([Q0]), "operationType" : NewBodyOperationType.ADD, "endBound" : BoundingType.SYMMETRIC, "depth" : 381 * mm, "offsetDistance" : 25.4 * mm});
        }
    });
